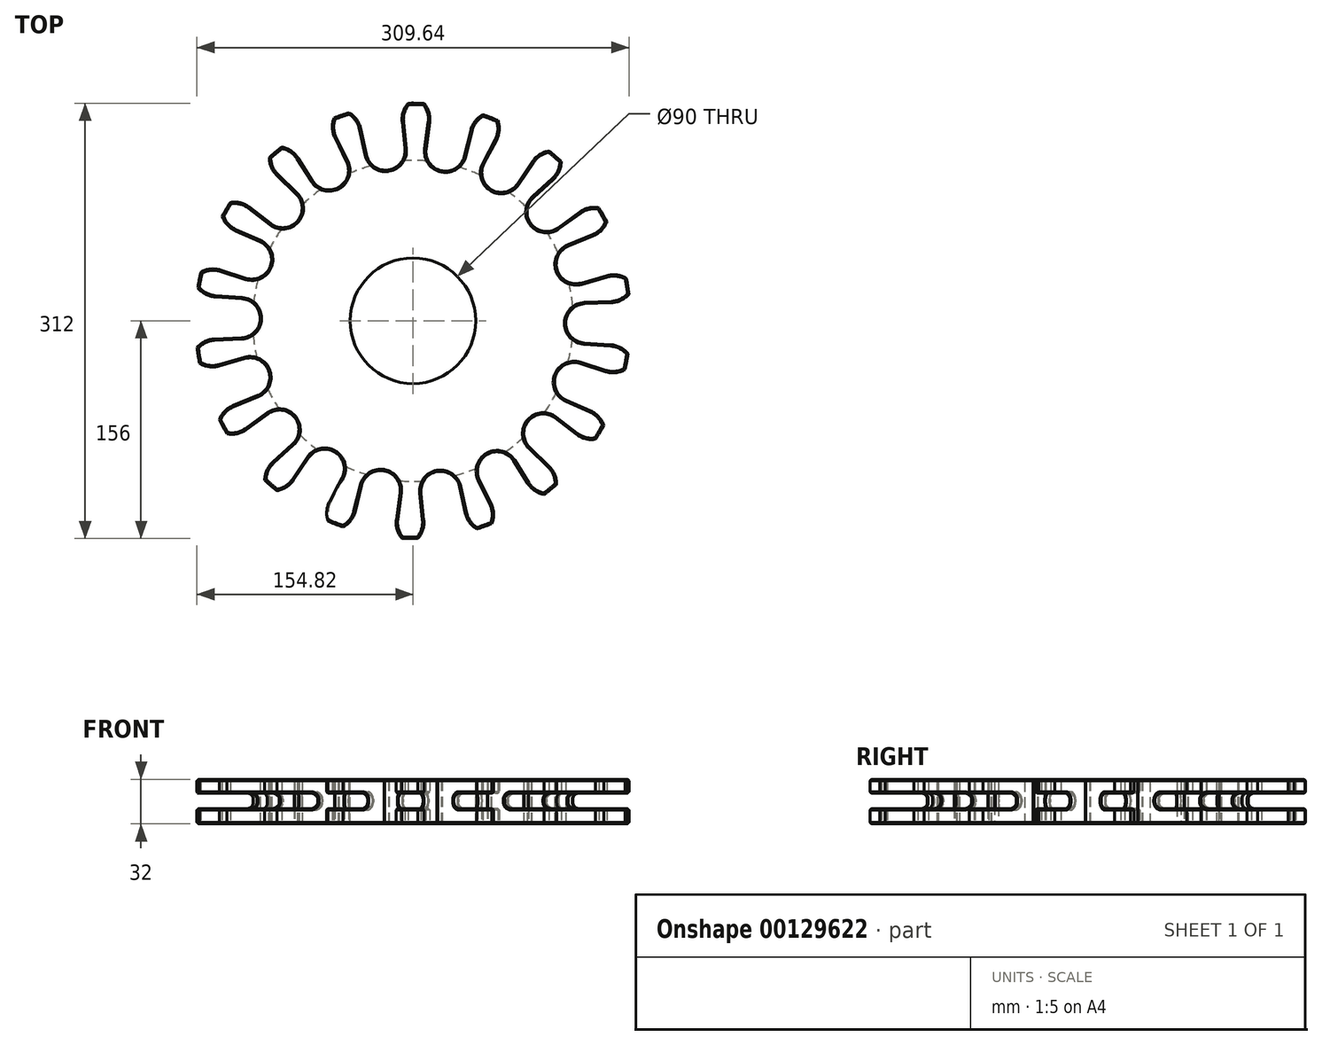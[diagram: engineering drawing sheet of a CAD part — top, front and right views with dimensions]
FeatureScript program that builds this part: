
annotation { "Feature Type Name" : "Feature", "Feature Type Description" : "" }
export const myFeature = defineFeature(function(context is Context, id is Id, definition is map)
    precondition{}
    {
        {
            var Q0;
            Q0=qCreatedBy(makeId("Top.planeOp"),FACE);
            var sketch = newSketch(context, id + "F0", { "sketchPlane" : qUnion([Q0])});
            skCircle(sketch, "E0", {"center": v(0, 0) * mm, "radius": 158.3 * mm, "construction": true});
            skArc(sketch, "E1", {"start": v(-102.28, 39.14) * mm, "mid": v(-102.55, 49.4) * mm, "end": v(-109.74, 56.72) * mm});
            skLineSegment(sketch, "E2", {"start": v(-109.74, 56.72) * mm, "end": v(-127.33, 64.55) * mm});
            skArc(sketch, "E3", {"start": v(-127.33, 64.55) * mm, "mid": v(-133.16, 68.77) * mm, "end": v(-136.8, 74.97) * mm});
            skArc(sketch, "E4", {"start": v(-136.8, 74.97) * mm, "mid": v(-133.95, 79.96) * mm, "end": v(-130.91, 84.84) * mm});
            skArc(sketch, "E5", {"start": v(-130.91, 84.84) * mm, "mid": v(-123.72, 84.58) * mm, "end": v(-117.25, 81.44) * mm});
            skLineSegment(sketch, "E6", {"start": v(-117.25, 81.44) * mm, "end": v(-102, 69.68) * mm});
            skArc(sketch, "E7", {"start": v(-102, 69.68) * mm, "mid": v(-92.15, 66.82) * mm, "end": v(-83, 71.46) * mm});
            skLineSegment(sketch, "E8", {"start": v(-83, 71.46) * mm, "end": v(-82.72, 71.76) * mm});
            skArc(sketch, "E9", {"start": v(-82.72, 71.76) * mm, "mid": v(-79.47, 81.5) * mm, "end": v(-83.72, 90.83) * mm});
            skLineSegment(sketch, "E10", {"start": v(-83.72, 90.83) * mm, "end": v(-97.57, 104.2) * mm});
            skArc(sketch, "E11", {"start": v(-97.57, 104.2) * mm, "mid": v(-101.6, 110.16) * mm, "end": v(-102.91, 117.24) * mm});
            skArc(sketch, "E12", {"start": v(-102.91, 117.24) * mm, "mid": v(-98.52, 120.95) * mm, "end": v(-94, 124.5) * mm});
            skArc(sketch, "E13", {"start": v(-94, 124.5) * mm, "mid": v(-87.33, 121.8) * mm, "end": v(-82.32, 116.63) * mm});
            skLineSegment(sketch, "E14", {"start": v(-82.32, 116.63) * mm, "end": v(-72.02, 100.36) * mm});
            skArc(sketch, "E15", {"start": v(-72.02, 100.36) * mm, "mid": v(-63.74, 94.31) * mm, "end": v(-53.55, 95.53) * mm});
            skLineSegment(sketch, "E16", {"start": v(-53.55, 95.53) * mm, "end": v(-53.2, 95.73) * mm});
            skArc(sketch, "E17", {"start": v(-53.2, 95.73) * mm, "mid": v(-46.8, 103.76) * mm, "end": v(-47.6, 113.99) * mm});
            skLineSegment(sketch, "E18", {"start": v(-47.6, 113.99) * mm, "end": v(-56.04, 131.3) * mm});
            skArc(sketch, "E19", {"start": v(-56.04, 131.3) * mm, "mid": v(-57.8, 138.27) * mm, "end": v(-56.6, 145.37) * mm});
            skArc(sketch, "E20", {"start": v(-56.6, 145.37) * mm, "mid": v(-51.21, 147.35) * mm, "end": v(-45.75, 149.14) * mm});
            skArc(sketch, "E21", {"start": v(-45.75, 149.14) * mm, "mid": v(-40.41, 144.32) * mm, "end": v(-37.46, 137.75) * mm});
            skLineSegment(sketch, "E22", {"start": v(-37.46, 137.75) * mm, "end": v(-33.35, 118.94) * mm});
            skArc(sketch, "E23", {"start": v(-33.35, 118.94) * mm, "mid": v(-27.64, 110.42) * mm, "end": v(-17.64, 108.08) * mm});
            skLineSegment(sketch, "E24", {"start": v(-17.64, 108.08) * mm, "end": v(-17.24, 108.15) * mm});
            skArc(sketch, "E25", {"start": v(-17.24, 108.15) * mm, "mid": v(-8.5, 113.5) * mm, "end": v(-5.75, 123.4) * mm});
            skLineSegment(sketch, "E26", {"start": v(-5.75, 123.4) * mm, "end": v(-7.76, 142.55) * mm});
            skArc(sketch, "E27", {"start": v(-7.76, 142.55) * mm, "mid": v(-7.02, 149.7) * mm, "end": v(-3.48, 155.96) * mm});
            skArc(sketch, "E28", {"start": v(-3.48, 155.96) * mm, "mid": v(2.27, 155.98) * mm, "end": v(8.02, 155.8) * mm});
            skArc(sketch, "E29", {"start": v(8.02, 155.8) * mm, "mid": v(11.38, 149.43) * mm, "end": v(11.9, 142.26) * mm});
            skLineSegment(sketch, "E30", {"start": v(11.9, 142.26) * mm, "end": v(9.34, 123.18) * mm});
            skArc(sketch, "E31", {"start": v(9.34, 123.18) * mm, "mid": v(11.8, 113.21) * mm, "end": v(20.39, 107.6) * mm});
            skLineSegment(sketch, "E32", {"start": v(20.39, 107.6) * mm, "end": v(20.79, 107.52) * mm});
            skArc(sketch, "E33", {"start": v(20.79, 107.52) * mm, "mid": v(30.84, 109.57) * mm, "end": v(36.8, 117.92) * mm});
            skLineSegment(sketch, "E34", {"start": v(36.8, 117.92) * mm, "end": v(41.46, 136.6) * mm});
            skArc(sketch, "E35", {"start": v(41.46, 136.6) * mm, "mid": v(44.6, 143.08) * mm, "end": v(50.07, 147.74) * mm});
            skArc(sketch, "E36", {"start": v(50.07, 147.74) * mm, "mid": v(55.49, 145.8) * mm, "end": v(60.82, 143.65) * mm});
            skArc(sketch, "E37", {"start": v(60.82, 143.65) * mm, "mid": v(61.8, 136.53) * mm, "end": v(59.85, 129.6) * mm});
            skLineSegment(sketch, "E38", {"start": v(59.85, 129.6) * mm, "end": v(50.9, 112.55) * mm});
            skArc(sketch, "E39", {"start": v(50.9, 112.55) * mm, "mid": v(49.8, 102.35) * mm, "end": v(55.96, 94.14) * mm});
            skLineSegment(sketch, "E40", {"start": v(55.96, 94.14) * mm, "end": v(56.3, 93.93) * mm});
            skArc(sketch, "E41", {"start": v(56.3, 93.93) * mm, "mid": v(66.46, 92.41) * mm, "end": v(74.91, 98.22) * mm});
            skLineSegment(sketch, "E42", {"start": v(74.91, 98.22) * mm, "end": v(85.68, 114.18) * mm});
            skArc(sketch, "E43", {"start": v(85.68, 114.18) * mm, "mid": v(90.85, 119.2) * mm, "end": v(97.59, 121.7) * mm});
            skArc(sketch, "E44", {"start": v(97.59, 121.7) * mm, "mid": v(102, 118.03) * mm, "end": v(106.29, 114.19) * mm});
            skArc(sketch, "E45", {"start": v(106.29, 114.19) * mm, "mid": v(104.77, 107.16) * mm, "end": v(100.56, 101.32) * mm});
            skLineSegment(sketch, "E46", {"start": v(100.56, 101.32) * mm, "end": v(86.33, 88.35) * mm});
            skArc(sketch, "E47", {"start": v(86.33, 88.35) * mm, "mid": v(81.8, 79.14) * mm, "end": v(84.78, 69.32) * mm});
            skLineSegment(sketch, "E48", {"start": v(84.78, 69.32) * mm, "end": v(85.04, 69) * mm});
            skArc(sketch, "E49", {"start": v(85.04, 69) * mm, "mid": v(94.06, 64.1) * mm, "end": v(104, 66.68) * mm});
            skLineSegment(sketch, "E50", {"start": v(104, 66.68) * mm, "end": v(119.57, 78) * mm});
            skArc(sketch, "E51", {"start": v(119.57, 78) * mm, "mid": v(126.13, 80.93) * mm, "end": v(133.33, 81) * mm});
            skArc(sketch, "E52", {"start": v(133.33, 81) * mm, "mid": v(136.22, 76.02) * mm, "end": v(138.93, 70.95) * mm});
            skArc(sketch, "E53", {"start": v(138.93, 70.95) * mm, "mid": v(135.1, 64.86) * mm, "end": v(129.15, 60.82) * mm});
            skLineSegment(sketch, "E54", {"start": v(129.15, 60.82) * mm, "end": v(111.35, 53.5) * mm});
            skArc(sketch, "E55", {"start": v(111.35, 53.5) * mm, "mid": v(103.94, 46.4) * mm, "end": v(103.38, 36.15) * mm});
            skLineSegment(sketch, "E56", {"start": v(103.38, 36.15) * mm, "end": v(103.51, 35.76) * mm});
            skArc(sketch, "E57", {"start": v(103.51, 35.76) * mm, "mid": v(110.31, 28.07) * mm, "end": v(120.52, 27.09) * mm});
            skLineSegment(sketch, "E58", {"start": v(120.52, 27.09) * mm, "end": v(139.03, 32.4) * mm});
            skArc(sketch, "E59", {"start": v(139.03, 32.4) * mm, "mid": v(146.2, 32.91) * mm, "end": v(152.99, 30.5) * mm});
            skArc(sketch, "E60", {"start": v(152.99, 30.5) * mm, "mid": v(154, 24.85) * mm, "end": v(154.82, 19.15) * mm});
            skArc(sketch, "E61", {"start": v(154.82, 19.15) * mm, "mid": v(149.14, 14.74) * mm, "end": v(142.17, 12.98) * mm});
            skLineSegment(sketch, "E62", {"start": v(142.17, 12.98) * mm, "end": v(122.93, 12.19) * mm});
            skArc(sketch, "E63", {"start": v(122.93, 12.19) * mm, "mid": v(113.54, 8.04) * mm, "end": v(109.5, -1.4) * mm});
            skLineSegment(sketch, "E64", {"start": v(109.5, -1.4) * mm, "end": v(109.5, -1.8) * mm});
            skArc(sketch, "E65", {"start": v(109.5, -1.8) * mm, "mid": v(113.26, -11.35) * mm, "end": v(122.52, -15.77) * mm});
            skLineSegment(sketch, "E66", {"start": v(122.52, -15.77) * mm, "end": v(141.73, -17.11) * mm});
            skArc(sketch, "E67", {"start": v(141.73, -17.11) * mm, "mid": v(148.65, -19.08) * mm, "end": v(154.2, -23.66) * mm});
            skArc(sketch, "E68", {"start": v(154.2, -23.66) * mm, "mid": v(153.22, -29.33) * mm, "end": v(152.03, -34.95) * mm});
            skArc(sketch, "E69", {"start": v(152.03, -34.95) * mm, "mid": v(145.19, -37.16) * mm, "end": v(138.03, -36.43) * mm});
            skLineSegment(sketch, "E70", {"start": v(138.03, -36.43) * mm, "end": v(119.68, -30.6) * mm});
            skArc(sketch, "E71", {"start": v(119.68, -30.6) * mm, "mid": v(109.45, -31.28) * mm, "end": v(102.43, -38.76) * mm});
            skLineSegment(sketch, "E72", {"start": v(102.43, -38.76) * mm, "end": v(102.28, -39.14) * mm});
            skArc(sketch, "E73", {"start": v(102.28, -39.14) * mm, "mid": v(102.55, -49.4) * mm, "end": v(109.74, -56.72) * mm});
            skLineSegment(sketch, "E74", {"start": v(109.74, -56.72) * mm, "end": v(127.33, -64.55) * mm});
            skArc(sketch, "E75", {"start": v(127.33, -64.55) * mm, "mid": v(133.16, -68.77) * mm, "end": v(136.8, -74.97) * mm});
            skArc(sketch, "E76", {"start": v(136.8, -74.97) * mm, "mid": v(133.95, -79.96) * mm, "end": v(130.91, -84.84) * mm});
            skArc(sketch, "E77", {"start": v(130.91, -84.84) * mm, "mid": v(123.72, -84.58) * mm, "end": v(117.25, -81.44) * mm});
            skLineSegment(sketch, "E78", {"start": v(117.25, -81.44) * mm, "end": v(102, -69.68) * mm});
            skArc(sketch, "E79", {"start": v(102, -69.68) * mm, "mid": v(92.15, -66.82) * mm, "end": v(83, -71.46) * mm});
            skLineSegment(sketch, "E80", {"start": v(83, -71.46) * mm, "end": v(82.72, -71.76) * mm});
            skArc(sketch, "E81", {"start": v(82.72, -71.76) * mm, "mid": v(79.47, -81.5) * mm, "end": v(83.72, -90.83) * mm});
            skLineSegment(sketch, "E82", {"start": v(83.72, -90.83) * mm, "end": v(97.57, -104.2) * mm});
            skArc(sketch, "E83", {"start": v(97.57, -104.2) * mm, "mid": v(101.6, -110.16) * mm, "end": v(102.91, -117.24) * mm});
            skArc(sketch, "E84", {"start": v(102.91, -117.24) * mm, "mid": v(98.52, -120.95) * mm, "end": v(94, -124.5) * mm});
            skArc(sketch, "E85", {"start": v(94, -124.5) * mm, "mid": v(87.33, -121.8) * mm, "end": v(82.32, -116.63) * mm});
            skLineSegment(sketch, "E86", {"start": v(82.32, -116.63) * mm, "end": v(72.02, -100.36) * mm});
            skArc(sketch, "E87", {"start": v(72.02, -100.36) * mm, "mid": v(63.74, -94.31) * mm, "end": v(53.55, -95.53) * mm});
            skLineSegment(sketch, "E88", {"start": v(53.55, -95.53) * mm, "end": v(53.2, -95.73) * mm});
            skArc(sketch, "E89", {"start": v(53.2, -95.73) * mm, "mid": v(46.8, -103.76) * mm, "end": v(47.6, -113.99) * mm});
            skLineSegment(sketch, "E90", {"start": v(47.6, -113.99) * mm, "end": v(56.04, -131.3) * mm});
            skArc(sketch, "E91", {"start": v(56.04, -131.3) * mm, "mid": v(57.8, -138.27) * mm, "end": v(56.6, -145.37) * mm});
            skArc(sketch, "E92", {"start": v(56.6, -145.37) * mm, "mid": v(51.21, -147.35) * mm, "end": v(45.75, -149.14) * mm});
            skArc(sketch, "E93", {"start": v(45.75, -149.14) * mm, "mid": v(40.41, -144.32) * mm, "end": v(37.46, -137.75) * mm});
            skLineSegment(sketch, "E94", {"start": v(37.46, -137.75) * mm, "end": v(33.35, -118.94) * mm});
            skArc(sketch, "E95", {"start": v(33.35, -118.94) * mm, "mid": v(27.64, -110.42) * mm, "end": v(17.64, -108.08) * mm});
            skLineSegment(sketch, "E96", {"start": v(17.64, -108.08) * mm, "end": v(17.24, -108.15) * mm});
            skArc(sketch, "E97", {"start": v(17.24, -108.15) * mm, "mid": v(8.5, -113.5) * mm, "end": v(5.75, -123.4) * mm});
            skLineSegment(sketch, "E98", {"start": v(5.75, -123.4) * mm, "end": v(7.76, -142.55) * mm});
            skArc(sketch, "E99", {"start": v(7.76, -142.55) * mm, "mid": v(7.02, -149.7) * mm, "end": v(3.48, -155.96) * mm});
            skArc(sketch, "E100", {"start": v(3.48, -155.96) * mm, "mid": v(-2.27, -155.98) * mm, "end": v(-8.02, -155.8) * mm});
            skArc(sketch, "E101", {"start": v(-8.02, -155.8) * mm, "mid": v(-11.38, -149.43) * mm, "end": v(-11.9, -142.26) * mm});
            skLineSegment(sketch, "E102", {"start": v(-11.9, -142.26) * mm, "end": v(-9.34, -123.18) * mm});
            skArc(sketch, "E103", {"start": v(-9.34, -123.18) * mm, "mid": v(-11.8, -113.21) * mm, "end": v(-20.39, -107.6) * mm});
            skLineSegment(sketch, "E104", {"start": v(-20.39, -107.6) * mm, "end": v(-20.79, -107.52) * mm});
            skArc(sketch, "E105", {"start": v(-20.79, -107.52) * mm, "mid": v(-30.84, -109.57) * mm, "end": v(-36.8, -117.92) * mm});
            skLineSegment(sketch, "E106", {"start": v(-36.8, -117.92) * mm, "end": v(-41.46, -136.6) * mm});
            skArc(sketch, "E107", {"start": v(-41.46, -136.6) * mm, "mid": v(-44.6, -143.08) * mm, "end": v(-50.07, -147.74) * mm});
            skArc(sketch, "E108", {"start": v(-50.07, -147.74) * mm, "mid": v(-55.49, -145.8) * mm, "end": v(-60.82, -143.65) * mm});
            skArc(sketch, "E109", {"start": v(-60.82, -143.65) * mm, "mid": v(-61.8, -136.53) * mm, "end": v(-59.85, -129.6) * mm});
            skLineSegment(sketch, "E110", {"start": v(-59.85, -129.6) * mm, "end": v(-50.9, -112.55) * mm});
            skArc(sketch, "E111", {"start": v(-50.9, -112.55) * mm, "mid": v(-49.8, -102.35) * mm, "end": v(-55.96, -94.14) * mm});
            skLineSegment(sketch, "E112", {"start": v(-55.96, -94.14) * mm, "end": v(-56.3, -93.93) * mm});
            skArc(sketch, "E113", {"start": v(-56.3, -93.93) * mm, "mid": v(-66.46, -92.41) * mm, "end": v(-74.91, -98.22) * mm});
            skLineSegment(sketch, "E114", {"start": v(-74.91, -98.22) * mm, "end": v(-85.68, -114.18) * mm});
            skArc(sketch, "E115", {"start": v(-85.68, -114.18) * mm, "mid": v(-90.85, -119.2) * mm, "end": v(-97.59, -121.7) * mm});
            skArc(sketch, "E116", {"start": v(-97.59, -121.7) * mm, "mid": v(-102, -118.03) * mm, "end": v(-106.29, -114.19) * mm});
            skArc(sketch, "E117", {"start": v(-106.29, -114.19) * mm, "mid": v(-104.77, -107.16) * mm, "end": v(-100.56, -101.32) * mm});
            skLineSegment(sketch, "E118", {"start": v(-100.56, -101.32) * mm, "end": v(-86.33, -88.35) * mm});
            skArc(sketch, "E119", {"start": v(-86.33, -88.35) * mm, "mid": v(-81.8, -79.14) * mm, "end": v(-84.78, -69.32) * mm});
            skLineSegment(sketch, "E120", {"start": v(-84.78, -69.32) * mm, "end": v(-85.04, -69) * mm});
            skArc(sketch, "E121", {"start": v(-85.04, -69) * mm, "mid": v(-94.06, -64.1) * mm, "end": v(-104, -66.68) * mm});
            skLineSegment(sketch, "E122", {"start": v(-104, -66.68) * mm, "end": v(-119.57, -78) * mm});
            skArc(sketch, "E123", {"start": v(-119.57, -78) * mm, "mid": v(-126.13, -80.93) * mm, "end": v(-133.33, -81) * mm});
            skArc(sketch, "E124", {"start": v(-133.33, -81) * mm, "mid": v(-136.22, -76.02) * mm, "end": v(-138.93, -70.95) * mm});
            skArc(sketch, "E125", {"start": v(-138.93, -70.95) * mm, "mid": v(-135.1, -64.86) * mm, "end": v(-129.15, -60.82) * mm});
            skLineSegment(sketch, "E126", {"start": v(-129.15, -60.82) * mm, "end": v(-111.35, -53.5) * mm});
            skArc(sketch, "E127", {"start": v(-111.35, -53.5) * mm, "mid": v(-103.94, -46.4) * mm, "end": v(-103.38, -36.15) * mm});
            skLineSegment(sketch, "E128", {"start": v(-103.38, -36.15) * mm, "end": v(-103.51, -35.76) * mm});
            skArc(sketch, "E129", {"start": v(-103.51, -35.76) * mm, "mid": v(-110.31, -28.07) * mm, "end": v(-120.52, -27.09) * mm});
            skLineSegment(sketch, "E130", {"start": v(-120.52, -27.09) * mm, "end": v(-139.03, -32.4) * mm});
            skArc(sketch, "E131", {"start": v(-139.03, -32.4) * mm, "mid": v(-146.2, -32.91) * mm, "end": v(-152.99, -30.5) * mm});
            skArc(sketch, "E132", {"start": v(-152.99, -30.5) * mm, "mid": v(-154, -24.85) * mm, "end": v(-154.82, -19.15) * mm});
            skArc(sketch, "E133", {"start": v(-154.82, -19.15) * mm, "mid": v(-149.14, -14.74) * mm, "end": v(-142.17, -12.98) * mm});
            skLineSegment(sketch, "E134", {"start": v(-142.17, -12.98) * mm, "end": v(-122.93, -12.19) * mm});
            skArc(sketch, "E135", {"start": v(-122.93, -12.19) * mm, "mid": v(-113.54, -8.04) * mm, "end": v(-109.5, 1.4) * mm});
            skLineSegment(sketch, "E136", {"start": v(-109.5, 1.4) * mm, "end": v(-109.5, 1.8) * mm});
            skArc(sketch, "E137", {"start": v(-109.5, 1.8) * mm, "mid": v(-113.26, 11.35) * mm, "end": v(-122.52, 15.77) * mm});
            skLineSegment(sketch, "E138", {"start": v(-122.52, 15.77) * mm, "end": v(-141.73, 17.11) * mm});
            skArc(sketch, "E139", {"start": v(-141.73, 17.11) * mm, "mid": v(-148.65, 19.08) * mm, "end": v(-154.2, 23.66) * mm});
            skArc(sketch, "E140", {"start": v(-154.2, 23.66) * mm, "mid": v(-153.22, 29.33) * mm, "end": v(-152.03, 34.95) * mm});
            skArc(sketch, "E141", {"start": v(-152.03, 34.95) * mm, "mid": v(-145.19, 37.16) * mm, "end": v(-138.03, 36.43) * mm});
            skLineSegment(sketch, "E142", {"start": v(-138.03, 36.43) * mm, "end": v(-119.68, 30.6) * mm});
            skArc(sketch, "E143", {"start": v(-119.68, 30.6) * mm, "mid": v(-109.45, 31.28) * mm, "end": v(-102.43, 38.76) * mm});
            skLineSegment(sketch, "E144", {"start": v(-102.43, 38.76) * mm, "end": v(-102.28, 39.14) * mm});
            skCircle(sketch, "E145", {"center": v(0, 0) * mm, "radius": 74.9 * mm, "construction": true});
            skSolve(sketch);
        }
        {
            var Q0;
            Q0 = qSketchRegion(id + "F0", true);
            extrude(context, id + "F1", {"entities" : qUnion([Q0]), "endBound" : BoundingType.SYMMETRIC, "depth" : 32 * mm});
        }
        {
            var Q0;
            Q0=qCreatedBy(makeId("Top.planeOp"),FACE);
            var sketch = newSketch(context, id + "F2", { "sketchPlane" : qUnion([Q0])});
            skCircle(sketch, "E146", {"center": v(0, 0) * mm, "radius": 45 * mm});
            skSolve(sketch);
        }
        {
            var Q0;
            Q0 = qSketchRegion(id + "F2", true);
            extrude(context, id + "F3", {"entities" : qUnion([Q0]), "operationType" : NewBodyOperationType.REMOVE, "endBound" : BoundingType.SYMMETRIC, "oppositeDirection" : true, "depth" : 91.5 * mm});
        }
        {
            var Q0;
            Q0=qCreatedBy(makeId("Right.planeOp"),FACE);
            var sketch = newSketch(context, id + "F4", { "sketchPlane" : qUnion([Q0])});
            skLineSegment(sketch, "E147.bottom", {"start": v(-163.5, 6) * mm, "end": v(-119.5, 6) * mm});
            skLineSegment(sketch, "E147.top", {"start": v(-163.5, -5) * mm, "end": v(-119.5, -5) * mm});
            skLineSegment(sketch, "E147.left", {"start": v(-163.5, 6) * mm, "end": v(-163.5, -5) * mm});
            skLineSegment(sketch, "E147.right", {"start": v(-115, 1.5) * mm, "end": v(-115, -0.5) * mm});
            skPoint(sketch, "E148.visualSharp", {"position": v(-115, 6) * mm});
            skArc(sketch, "E148.filletArc", {"start": v(-115, 1.5) * mm, "mid": v(-116.32, 4.68) * mm, "end": v(-119.5, 6) * mm});
            skPoint(sketch, "E149.visualSharp", {"position": v(-115, -5) * mm});
            skArc(sketch, "E149.filletArc", {"start": v(-119.5, -5) * mm, "mid": v(-116.32, -3.68) * mm, "end": v(-115, -0.5) * mm});
            skSolve(sketch);
        }
        {
            var Q0;
            Q0 = qSketchRegion(id + "F4", true);
            var Q1;
            Q1=makeQuery(id+"F3.boolean.opBoolean","COPY",FACE,{"derivedFrom":makeQuery(id+"F3.opExtrude","SWEPT_FACE",FACE,{"disambiguationData":[OSD([sQuery(id+"F2.wireOp",EDGE,"E146")])]})});
            revolve(context, id + "F5", {"operationType" : NewBodyOperationType.REMOVE, "entities" : qUnion([Q0]), "axis" : qUnion([Q1]), "revolveType" : RevolveType.FULL, "oppositeDirection" : true});
        }
        {
            var Q0;
            Q0=makeQuery(id+"F1.opExtrude","CAP_EDGE",EDGE,{"disambiguationData":[OSD([sQuery(id+"F0.wireOp",EDGE,"E113")])],"isStart":false});
            var Q1;
            Q1=makeQuery(id+"F1.opExtrude","CAP_EDGE",EDGE,{"disambiguationData":[OSD([sQuery(id+"F0.wireOp",EDGE,"E121")])],"isStart":false});
            var Q2;
            Q2=makeQuery(id+"F1.opExtrude","CAP_EDGE",EDGE,{"disambiguationData":[OSD([sQuery(id+"F0.wireOp",EDGE,"E129")])],"isStart":false});
            var Q3;
            Q3=makeQuery(id+"F1.opExtrude","CAP_EDGE",EDGE,{"disambiguationData":[OSD([sQuery(id+"F0.wireOp",EDGE,"E137")])],"isStart":false});
            var Q4;
            Q4=makeQuery(id+"F1.opExtrude","CAP_EDGE",EDGE,{"disambiguationData":[OSD([sQuery(id+"F0.wireOp",EDGE,"E1")])],"isStart":false});
            var Q5;
            Q5=makeQuery(id+"F1.opExtrude","CAP_EDGE",EDGE,{"disambiguationData":[OSD([sQuery(id+"F0.wireOp",EDGE,"E9")])],"isStart":false});
            var Q6;
            Q6=makeQuery(id+"F1.opExtrude","CAP_EDGE",EDGE,{"disambiguationData":[OSD([sQuery(id+"F0.wireOp",EDGE,"E17")])],"isStart":false});
            var Q7;
            Q7=makeQuery(id+"F1.opExtrude","CAP_EDGE",EDGE,{"disambiguationData":[OSD([sQuery(id+"F0.wireOp",EDGE,"E25")])],"isStart":false});
            var Q8;
            Q8=makeQuery(id+"F1.opExtrude","CAP_EDGE",EDGE,{"disambiguationData":[OSD([sQuery(id+"F0.wireOp",EDGE,"E33")])],"isStart":false});
            var Q9;
            Q9=makeQuery(id+"F1.opExtrude","CAP_EDGE",EDGE,{"disambiguationData":[OSD([sQuery(id+"F0.wireOp",EDGE,"E41")])],"isStart":false});
            var Q10;
            Q10=makeQuery(id+"F1.opExtrude","CAP_EDGE",EDGE,{"disambiguationData":[OSD([sQuery(id+"F0.wireOp",EDGE,"E50")])],"isStart":false});
            var Q11;
            Q11=makeQuery(id+"F1.opExtrude","CAP_EDGE",EDGE,{"disambiguationData":[OSD([sQuery(id+"F0.wireOp",EDGE,"E58")])],"isStart":false});
            var Q12;
            Q12=makeQuery(id+"F1.opExtrude","CAP_EDGE",EDGE,{"disambiguationData":[OSD([sQuery(id+"F0.wireOp",EDGE,"E65")])],"isStart":false});
            var Q13;
            Q13=makeQuery(id+"F1.opExtrude","CAP_EDGE",EDGE,{"disambiguationData":[OSD([sQuery(id+"F0.wireOp",EDGE,"E73")])],"isStart":false});
            var Q14;
            Q14=makeQuery(id+"F1.opExtrude","CAP_EDGE",EDGE,{"disambiguationData":[OSD([sQuery(id+"F0.wireOp",EDGE,"E81")])],"isStart":false});
            var Q15;
            Q15=makeQuery(id+"F1.opExtrude","CAP_EDGE",EDGE,{"disambiguationData":[OSD([sQuery(id+"F0.wireOp",EDGE,"E89")])],"isStart":false});
            var Q16;
            Q16=makeQuery(id+"F1.opExtrude","CAP_EDGE",EDGE,{"disambiguationData":[OSD([sQuery(id+"F0.wireOp",EDGE,"E97")])],"isStart":false});
            var Q17;
            Q17=makeQuery(id+"F1.opExtrude","CAP_EDGE",EDGE,{"disambiguationData":[OSD([sQuery(id+"F0.wireOp",EDGE,"E105")])],"isStart":false});
            var Q18;
            Q18=makeQuery(id+"F1.opExtrude","CAP_EDGE",EDGE,{"disambiguationData":[OSD([sQuery(id+"F0.wireOp",EDGE,"E103")])],"isStart":false});
            var Q19;
            Q19=makeQuery(id+"F1.opExtrude","CAP_EDGE",EDGE,{"disambiguationData":[OSD([sQuery(id+"F0.wireOp",EDGE,"E95")])],"isStart":false});
            var Q20;
            Q20=makeQuery(id+"F1.opExtrude","CAP_EDGE",EDGE,{"disambiguationData":[OSD([sQuery(id+"F0.wireOp",EDGE,"E87")])],"isStart":false});
            var Q21;
            Q21=makeQuery(id+"F1.opExtrude","CAP_EDGE",EDGE,{"disambiguationData":[OSD([sQuery(id+"F0.wireOp",EDGE,"E79")])],"isStart":false});
            var Q22;
            Q22=makeQuery(id+"F1.opExtrude","CAP_EDGE",EDGE,{"disambiguationData":[OSD([sQuery(id+"F0.wireOp",EDGE,"E71")])],"isStart":false});
            var Q23;
            Q23=makeQuery(id+"F1.opExtrude","CAP_EDGE",EDGE,{"disambiguationData":[OSD([sQuery(id+"F0.wireOp",EDGE,"E63")])],"isStart":false});
            var Q24;
            Q24=makeQuery(id+"F1.opExtrude","CAP_EDGE",EDGE,{"disambiguationData":[OSD([sQuery(id+"F0.wireOp",EDGE,"E55")])],"isStart":false});
            var Q25;
            Q25=makeQuery(id+"F1.opExtrude","CAP_EDGE",EDGE,{"disambiguationData":[OSD([sQuery(id+"F0.wireOp",EDGE,"E47")])],"isStart":false});
            var Q26;
            Q26=makeQuery(id+"F1.opExtrude","CAP_EDGE",EDGE,{"disambiguationData":[OSD([sQuery(id+"F0.wireOp",EDGE,"E119")])],"isStart":false});
            var Q27;
            Q27=makeQuery(id+"F1.opExtrude","CAP_EDGE",EDGE,{"disambiguationData":[OSD([sQuery(id+"F0.wireOp",EDGE,"E127")])],"isStart":false});
            var Q28;
            Q28=makeQuery(id+"F1.opExtrude","CAP_EDGE",EDGE,{"disambiguationData":[OSD([sQuery(id+"F0.wireOp",EDGE,"E135")])],"isStart":false});
            var Q29;
            Q29=makeQuery(id+"F1.opExtrude","CAP_EDGE",EDGE,{"disambiguationData":[OSD([sQuery(id+"F0.wireOp",EDGE,"E143")])],"isStart":false});
            var Q30;
            Q30=makeQuery(id+"F1.opExtrude","CAP_EDGE",EDGE,{"disambiguationData":[OSD([sQuery(id+"F0.wireOp",EDGE,"E7")])],"isStart":false});
            var Q31;
            Q31=makeQuery(id+"F1.opExtrude","CAP_EDGE",EDGE,{"disambiguationData":[OSD([sQuery(id+"F0.wireOp",EDGE,"E15")])],"isStart":false});
            var Q32;
            Q32=makeQuery(id+"F1.opExtrude","CAP_EDGE",EDGE,{"disambiguationData":[OSD([sQuery(id+"F0.wireOp",EDGE,"E23")])],"isStart":false});
            var Q33;
            Q33=makeQuery(id+"F1.opExtrude","CAP_EDGE",EDGE,{"disambiguationData":[OSD([sQuery(id+"F0.wireOp",EDGE,"E31")])],"isStart":false});
            var Q34;
            Q34=makeQuery(id+"F1.opExtrude","CAP_EDGE",EDGE,{"disambiguationData":[OSD([sQuery(id+"F0.wireOp",EDGE,"E39")])],"isStart":false});
            var Q35;
            Q35=makeQuery(id+"F1.opExtrude","CAP_EDGE",EDGE,{"disambiguationData":[OSD([sQuery(id+"F0.wireOp",EDGE,"E100")])],"isStart":false});
            var Q36;
            Q36=makeQuery(id+"F1.opExtrude","CAP_EDGE",EDGE,{"disambiguationData":[OSD([sQuery(id+"F0.wireOp",EDGE,"E108")])],"isStart":false});
            var Q37;
            Q37=makeQuery(id+"F1.opExtrude","CAP_EDGE",EDGE,{"disambiguationData":[OSD([sQuery(id+"F0.wireOp",EDGE,"E116")])],"isStart":false});
            var Q38;
            Q38=makeQuery(id+"F1.opExtrude","CAP_EDGE",EDGE,{"disambiguationData":[OSD([sQuery(id+"F0.wireOp",EDGE,"E124")])],"isStart":false});
            var Q39;
            Q39=makeQuery(id+"F1.opExtrude","CAP_EDGE",EDGE,{"disambiguationData":[OSD([sQuery(id+"F0.wireOp",EDGE,"E132")])],"isStart":false});
            var Q40;
            Q40=makeQuery(id+"F1.opExtrude","CAP_EDGE",EDGE,{"disambiguationData":[OSD([sQuery(id+"F0.wireOp",EDGE,"E140")])],"isStart":false});
            var Q41;
            Q41=makeQuery(id+"F1.opExtrude","CAP_EDGE",EDGE,{"disambiguationData":[OSD([sQuery(id+"F0.wireOp",EDGE,"E4")])],"isStart":false});
            var Q42;
            Q42=makeQuery(id+"F1.opExtrude","CAP_EDGE",EDGE,{"disambiguationData":[OSD([sQuery(id+"F0.wireOp",EDGE,"E12")])],"isStart":false});
            var Q43;
            Q43=makeQuery(id+"F1.opExtrude","CAP_EDGE",EDGE,{"disambiguationData":[OSD([sQuery(id+"F0.wireOp",EDGE,"E20")])],"isStart":false});
            var Q44;
            Q44=makeQuery(id+"F1.opExtrude","CAP_EDGE",EDGE,{"disambiguationData":[OSD([sQuery(id+"F0.wireOp",EDGE,"E28")])],"isStart":false});
            var Q45;
            Q45=makeQuery(id+"F1.opExtrude","CAP_EDGE",EDGE,{"disambiguationData":[OSD([sQuery(id+"F0.wireOp",EDGE,"E36")])],"isStart":false});
            var Q46;
            Q46=makeQuery(id+"F1.opExtrude","CAP_EDGE",EDGE,{"disambiguationData":[OSD([sQuery(id+"F0.wireOp",EDGE,"E44")])],"isStart":false});
            var Q47;
            Q47=makeQuery(id+"F1.opExtrude","CAP_EDGE",EDGE,{"disambiguationData":[OSD([sQuery(id+"F0.wireOp",EDGE,"E52")])],"isStart":false});
            var Q48;
            Q48=makeQuery(id+"F1.opExtrude","CAP_EDGE",EDGE,{"disambiguationData":[OSD([sQuery(id+"F0.wireOp",EDGE,"E60")])],"isStart":false});
            var Q49;
            Q49=makeQuery(id+"F1.opExtrude","CAP_EDGE",EDGE,{"disambiguationData":[OSD([sQuery(id+"F0.wireOp",EDGE,"E68")])],"isStart":false});
            var Q50;
            Q50=makeQuery(id+"F1.opExtrude","CAP_EDGE",EDGE,{"disambiguationData":[OSD([sQuery(id+"F0.wireOp",EDGE,"E76")])],"isStart":false});
            var Q51;
            Q51=makeQuery(id+"F1.opExtrude","CAP_EDGE",EDGE,{"disambiguationData":[OSD([sQuery(id+"F0.wireOp",EDGE,"E84")])],"isStart":false});
            var Q52;
            Q52=makeQuery(id+"F1.opExtrude","CAP_EDGE",EDGE,{"disambiguationData":[OSD([sQuery(id+"F0.wireOp",EDGE,"E92")])],"isStart":false});
            var Q53;
            Q53=makeQuery(id+"F5.boolean.opBoolean","INTERSECT",EDGE,{"derivedFrom":[makeQuery(id+"F1.opExtrude","SWEPT_FACE",FACE,{"disambiguationData":[OSD([sQuery(id+"F0.wireOp",EDGE,"E89")])]}),makeQuery(id+"F5.opRevolve","SWEPT_FACE",FACE,{"disambiguationData":[OSD([sQuery(id+"F4.wireOp",EDGE,"E149.filletArc")])]})]});
            var Q54;
            Q54=makeQuery(id+"F5.boolean.opBoolean","INTERSECT",EDGE,{"derivedFrom":[makeQuery(id+"F1.opExtrude","SWEPT_FACE",FACE,{"disambiguationData":[OSD([sQuery(id+"F0.wireOp",EDGE,"E81")])]}),makeQuery(id+"F5.opRevolve","SWEPT_FACE",FACE,{"disambiguationData":[OSD([sQuery(id+"F4.wireOp",EDGE,"E149.filletArc")])]})]});
            var Q55;
            Q55=makeQuery(id+"F5.boolean.opBoolean","INTERSECT",EDGE,{"derivedFrom":[makeQuery(id+"F1.opExtrude","SWEPT_FACE",FACE,{"disambiguationData":[OSD([sQuery(id+"F0.wireOp",EDGE,"E79")])]}),makeQuery(id+"F5.opRevolve","SWEPT_FACE",FACE,{"disambiguationData":[OSD([sQuery(id+"F4.wireOp",EDGE,"E149.filletArc")])]})]});
            var Q56;
            Q56=makeQuery(id+"F5.boolean.opBoolean","INTERSECT",EDGE,{"derivedFrom":[makeQuery(id+"F1.opExtrude","SWEPT_FACE",FACE,{"disambiguationData":[OSD([sQuery(id+"F0.wireOp",EDGE,"E87")])]}),makeQuery(id+"F5.opRevolve","SWEPT_FACE",FACE,{"disambiguationData":[OSD([sQuery(id+"F4.wireOp",EDGE,"E149.filletArc")])]})]});
            var Q57;
            Q57=makeQuery(id+"F5.boolean.opBoolean","INTERSECT",EDGE,{"derivedFrom":[makeQuery(id+"F1.opExtrude","SWEPT_FACE",FACE,{"disambiguationData":[OSD([sQuery(id+"F0.wireOp",EDGE,"E95")])]}),makeQuery(id+"F5.opRevolve","SWEPT_FACE",FACE,{"disambiguationData":[OSD([sQuery(id+"F4.wireOp",EDGE,"E149.filletArc")])]})]});
            var Q58;
            Q58=makeQuery(id+"F5.boolean.opBoolean","INTERSECT",EDGE,{"derivedFrom":[makeQuery(id+"F1.opExtrude","SWEPT_FACE",FACE,{"disambiguationData":[OSD([sQuery(id+"F0.wireOp",EDGE,"E97")])]}),makeQuery(id+"F5.opRevolve","SWEPT_FACE",FACE,{"disambiguationData":[OSD([sQuery(id+"F4.wireOp",EDGE,"E149.filletArc")])]})]});
            var Q59;
            Q59=makeQuery(id+"F5.boolean.opBoolean","INTERSECT",EDGE,{"derivedFrom":[makeQuery(id+"F1.opExtrude","SWEPT_FACE",FACE,{"disambiguationData":[OSD([sQuery(id+"F0.wireOp",EDGE,"E105")])]}),makeQuery(id+"F5.opRevolve","SWEPT_FACE",FACE,{"disambiguationData":[OSD([sQuery(id+"F4.wireOp",EDGE,"E149.filletArc")])]})]});
            var Q60;
            Q60=makeQuery(id+"F5.boolean.opBoolean","INTERSECT",EDGE,{"derivedFrom":[makeQuery(id+"F1.opExtrude","SWEPT_FACE",FACE,{"disambiguationData":[OSD([sQuery(id+"F0.wireOp",EDGE,"E103")])]}),makeQuery(id+"F5.opRevolve","SWEPT_FACE",FACE,{"disambiguationData":[OSD([sQuery(id+"F4.wireOp",EDGE,"E149.filletArc")])]})]});
            var Q61;
            Q61=makeQuery(id+"F5.boolean.opBoolean","INTERSECT",EDGE,{"derivedFrom":[makeQuery(id+"F1.opExtrude","SWEPT_FACE",FACE,{"disambiguationData":[OSD([sQuery(id+"F0.wireOp",EDGE,"E111")])]}),makeQuery(id+"F5.opRevolve","SWEPT_FACE",FACE,{"disambiguationData":[OSD([sQuery(id+"F4.wireOp",EDGE,"E149.filletArc")])]})]});
            var Q62;
            Q62=makeQuery(id+"F5.boolean.opBoolean","INTERSECT",EDGE,{"derivedFrom":[makeQuery(id+"F1.opExtrude","SWEPT_FACE",FACE,{"disambiguationData":[OSD([sQuery(id+"F0.wireOp",EDGE,"E119")])]}),makeQuery(id+"F5.opRevolve","SWEPT_FACE",FACE,{"disambiguationData":[OSD([sQuery(id+"F4.wireOp",EDGE,"E149.filletArc")])]})]});
            var Q63;
            Q63=makeQuery(id+"F5.boolean.opBoolean","INTERSECT",EDGE,{"derivedFrom":[makeQuery(id+"F1.opExtrude","SWEPT_FACE",FACE,{"disambiguationData":[OSD([sQuery(id+"F0.wireOp",EDGE,"E121")])]}),makeQuery(id+"F5.opRevolve","SWEPT_FACE",FACE,{"disambiguationData":[OSD([sQuery(id+"F4.wireOp",EDGE,"E149.filletArc")])]})]});
            var Q64;
            Q64=makeQuery(id+"F5.boolean.opBoolean","INTERSECT",EDGE,{"derivedFrom":[makeQuery(id+"F1.opExtrude","SWEPT_FACE",FACE,{"disambiguationData":[OSD([sQuery(id+"F0.wireOp",EDGE,"E113")])]}),makeQuery(id+"F5.opRevolve","SWEPT_FACE",FACE,{"disambiguationData":[OSD([sQuery(id+"F4.wireOp",EDGE,"E149.filletArc")])]})]});
            var Q65;
            Q65=makeQuery(id+"F5.boolean.opBoolean","INTERSECT",EDGE,{"derivedFrom":[makeQuery(id+"F1.opExtrude","SWEPT_FACE",FACE,{"disambiguationData":[OSD([sQuery(id+"F0.wireOp",EDGE,"E129")])]}),makeQuery(id+"F5.opRevolve","SWEPT_FACE",FACE,{"disambiguationData":[OSD([sQuery(id+"F4.wireOp",EDGE,"E149.filletArc")])]})]});
            var Q66;
            Q66=makeQuery(id+"F5.boolean.opBoolean","INTERSECT",EDGE,{"derivedFrom":[makeQuery(id+"F1.opExtrude","SWEPT_FACE",FACE,{"disambiguationData":[OSD([sQuery(id+"F0.wireOp",EDGE,"E137")])]}),makeQuery(id+"F5.opRevolve","SWEPT_FACE",FACE,{"disambiguationData":[OSD([sQuery(id+"F4.wireOp",EDGE,"E149.filletArc")])]})]});
            var Q67;
            Q67=makeQuery(id+"F5.boolean.opBoolean","INTERSECT",EDGE,{"derivedFrom":[makeQuery(id+"F1.opExtrude","SWEPT_FACE",FACE,{"disambiguationData":[OSD([sQuery(id+"F0.wireOp",EDGE,"E127")])]}),makeQuery(id+"F5.opRevolve","SWEPT_FACE",FACE,{"disambiguationData":[OSD([sQuery(id+"F4.wireOp",EDGE,"E149.filletArc")])]})]});
            var Q68;
            Q68=makeQuery(id+"F5.boolean.opBoolean","INTERSECT",EDGE,{"derivedFrom":[makeQuery(id+"F1.opExtrude","SWEPT_FACE",FACE,{"disambiguationData":[OSD([sQuery(id+"F0.wireOp",EDGE,"E135")])]}),makeQuery(id+"F5.opRevolve","SWEPT_FACE",FACE,{"disambiguationData":[OSD([sQuery(id+"F4.wireOp",EDGE,"E149.filletArc")])]})]});
            var Q69;
            Q69=makeQuery(id+"F5.boolean.opBoolean","INTERSECT",EDGE,{"derivedFrom":[makeQuery(id+"F1.opExtrude","SWEPT_FACE",FACE,{"disambiguationData":[OSD([sQuery(id+"F0.wireOp",EDGE,"E7")])]}),makeQuery(id+"F5.opRevolve","SWEPT_FACE",FACE,{"disambiguationData":[OSD([sQuery(id+"F4.wireOp",EDGE,"E149.filletArc")])]})]});
            var Q70;
            Q70=makeQuery(id+"F5.boolean.opBoolean","INTERSECT",EDGE,{"derivedFrom":[makeQuery(id+"F1.opExtrude","SWEPT_FACE",FACE,{"disambiguationData":[OSD([sQuery(id+"F0.wireOp",EDGE,"E143")])]}),makeQuery(id+"F5.opRevolve","SWEPT_FACE",FACE,{"disambiguationData":[OSD([sQuery(id+"F4.wireOp",EDGE,"E149.filletArc")])]})]});
            var Q71;
            Q71=makeQuery(id+"F5.boolean.opBoolean","INTERSECT",EDGE,{"derivedFrom":[makeQuery(id+"F1.opExtrude","SWEPT_FACE",FACE,{"disambiguationData":[OSD([sQuery(id+"F0.wireOp",EDGE,"E17")])]}),makeQuery(id+"F5.opRevolve","SWEPT_FACE",FACE,{"disambiguationData":[OSD([sQuery(id+"F4.wireOp",EDGE,"E149.filletArc")])]})]});
            var Q72;
            Q72=makeQuery(id+"F5.boolean.opBoolean","INTERSECT",EDGE,{"derivedFrom":[makeQuery(id+"F1.opExtrude","SWEPT_FACE",FACE,{"disambiguationData":[OSD([sQuery(id+"F0.wireOp",EDGE,"E9")])]}),makeQuery(id+"F5.opRevolve","SWEPT_FACE",FACE,{"disambiguationData":[OSD([sQuery(id+"F4.wireOp",EDGE,"E149.filletArc")])]})]});
            var Q73;
            Q73=makeQuery(id+"F5.boolean.opBoolean","INTERSECT",EDGE,{"derivedFrom":[makeQuery(id+"F1.opExtrude","SWEPT_FACE",FACE,{"disambiguationData":[OSD([sQuery(id+"F0.wireOp",EDGE,"E1")])]}),makeQuery(id+"F5.opRevolve","SWEPT_FACE",FACE,{"disambiguationData":[OSD([sQuery(id+"F4.wireOp",EDGE,"E149.filletArc")])]})]});
            var Q74;
            Q74=makeQuery(id+"F5.boolean.opBoolean","INTERSECT",EDGE,{"derivedFrom":[makeQuery(id+"F1.opExtrude","SWEPT_FACE",FACE,{"disambiguationData":[OSD([sQuery(id+"F0.wireOp",EDGE,"E124")])]}),makeQuery(id+"F5.opRevolve","SWEPT_FACE",FACE,{"disambiguationData":[OSD([sQuery(id+"F4.wireOp",EDGE,"E147.top")])]})]});
            var Q75;
            Q75=makeQuery(id+"F5.boolean.opBoolean","INTERSECT",EDGE,{"derivedFrom":[makeQuery(id+"F1.opExtrude","SWEPT_FACE",FACE,{"disambiguationData":[OSD([sQuery(id+"F0.wireOp",EDGE,"E132")])]}),makeQuery(id+"F5.opRevolve","SWEPT_FACE",FACE,{"disambiguationData":[OSD([sQuery(id+"F4.wireOp",EDGE,"E147.top")])]})]});
            var Q76;
            Q76=makeQuery(id+"F5.boolean.opBoolean","INTERSECT",EDGE,{"derivedFrom":[makeQuery(id+"F1.opExtrude","SWEPT_FACE",FACE,{"disambiguationData":[OSD([sQuery(id+"F0.wireOp",EDGE,"E124")])]}),makeQuery(id+"F5.opRevolve","SWEPT_FACE",FACE,{"disambiguationData":[OSD([sQuery(id+"F4.wireOp",EDGE,"E147.bottom")])]})]});
            var Q77;
            Q77=makeQuery(id+"F5.boolean.opBoolean","INTERSECT",EDGE,{"derivedFrom":[makeQuery(id+"F1.opExtrude","SWEPT_FACE",FACE,{"disambiguationData":[OSD([sQuery(id+"F0.wireOp",EDGE,"E116")])]}),makeQuery(id+"F5.opRevolve","SWEPT_FACE",FACE,{"disambiguationData":[OSD([sQuery(id+"F4.wireOp",EDGE,"E147.top")])]})]});
            var Q78;
            Q78=makeQuery(id+"F5.boolean.opBoolean","INTERSECT",EDGE,{"derivedFrom":[makeQuery(id+"F1.opExtrude","SWEPT_FACE",FACE,{"disambiguationData":[OSD([sQuery(id+"F0.wireOp",EDGE,"E116")])]}),makeQuery(id+"F5.opRevolve","SWEPT_FACE",FACE,{"disambiguationData":[OSD([sQuery(id+"F4.wireOp",EDGE,"E147.bottom")])]})]});
            var Q79;
            Q79=makeQuery(id+"F5.boolean.opBoolean","INTERSECT",EDGE,{"derivedFrom":[makeQuery(id+"F1.opExtrude","SWEPT_FACE",FACE,{"disambiguationData":[OSD([sQuery(id+"F0.wireOp",EDGE,"E108")])]}),makeQuery(id+"F5.opRevolve","SWEPT_FACE",FACE,{"disambiguationData":[OSD([sQuery(id+"F4.wireOp",EDGE,"E147.top")])]})]});
            var Q80;
            Q80=makeQuery(id+"F5.boolean.opBoolean","INTERSECT",EDGE,{"derivedFrom":[makeQuery(id+"F1.opExtrude","SWEPT_FACE",FACE,{"disambiguationData":[OSD([sQuery(id+"F0.wireOp",EDGE,"E108")])]}),makeQuery(id+"F5.opRevolve","SWEPT_FACE",FACE,{"disambiguationData":[OSD([sQuery(id+"F4.wireOp",EDGE,"E147.bottom")])]})]});
            var Q81;
            Q81=makeQuery(id+"F1.opExtrude","CAP_EDGE",EDGE,{"disambiguationData":[OSD([sQuery(id+"F0.wireOp",EDGE,"E72")])],"isStart":false});
            var Q82;
            Q82=makeQuery(id+"F1.opExtrude","CAP_EDGE",EDGE,{"disambiguationData":[OSD([sQuery(id+"F0.wireOp",EDGE,"E64")])],"isStart":false});
            var Q83;
            Q83=makeQuery(id+"F1.opExtrude","CAP_EDGE",EDGE,{"disambiguationData":[OSD([sQuery(id+"F0.wireOp",EDGE,"E56")])],"isStart":false});
            var Q84;
            Q84=makeQuery(id+"F5.boolean.opBoolean","INTERSECT",EDGE,{"derivedFrom":[makeQuery(id+"F1.opExtrude","SWEPT_FACE",FACE,{"disambiguationData":[OSD([sQuery(id+"F0.wireOp",EDGE,"E55")])]}),makeQuery(id+"F5.opRevolve","SWEPT_FACE",FACE,{"disambiguationData":[OSD([sQuery(id+"F4.wireOp",EDGE,"E149.filletArc")])]})]});
            var Q85;
            Q85=makeQuery(id+"F5.boolean.opBoolean","INTERSECT",EDGE,{"derivedFrom":[makeQuery(id+"F1.opExtrude","SWEPT_FACE",FACE,{"disambiguationData":[OSD([sQuery(id+"F0.wireOp",EDGE,"E47")])]}),makeQuery(id+"F5.opRevolve","SWEPT_FACE",FACE,{"disambiguationData":[OSD([sQuery(id+"F4.wireOp",EDGE,"E149.filletArc")])]})]});
            var Q86;
            Q86=makeQuery(id+"F5.boolean.opBoolean","INTERSECT",EDGE,{"derivedFrom":[makeQuery(id+"F1.opExtrude","SWEPT_FACE",FACE,{"disambiguationData":[OSD([sQuery(id+"F0.wireOp",EDGE,"E63")])]}),makeQuery(id+"F5.opRevolve","SWEPT_FACE",FACE,{"disambiguationData":[OSD([sQuery(id+"F4.wireOp",EDGE,"E149.filletArc")])]})]});
            var Q87;
            Q87=makeQuery(id+"F5.boolean.opBoolean","INTERSECT",EDGE,{"derivedFrom":[makeQuery(id+"F1.opExtrude","SWEPT_FACE",FACE,{"disambiguationData":[OSD([sQuery(id+"F0.wireOp",EDGE,"E71")])]}),makeQuery(id+"F5.opRevolve","SWEPT_FACE",FACE,{"disambiguationData":[OSD([sQuery(id+"F4.wireOp",EDGE,"E149.filletArc")])]})]});
            var Q88;
            Q88=makeQuery(id+"F1.opExtrude","CAP_EDGE",EDGE,{"disambiguationData":[OSD([sQuery(id+"F0.wireOp",EDGE,"E16")])],"isStart":false});
            var Q89;
            Q89=makeQuery(id+"F1.opExtrude","CAP_EDGE",EDGE,{"disambiguationData":[OSD([sQuery(id+"F0.wireOp",EDGE,"E24")])],"isStart":false});
            var Q90;
            Q90=makeQuery(id+"F1.opExtrude","CAP_EDGE",EDGE,{"disambiguationData":[OSD([sQuery(id+"F0.wireOp",EDGE,"E32")])],"isStart":false});
            var Q91;
            Q91=makeQuery(id+"F1.opExtrude","CAP_EDGE",EDGE,{"disambiguationData":[OSD([sQuery(id+"F0.wireOp",EDGE,"E40")])],"isStart":false});
            var Q92;
            Q92=makeQuery(id+"F1.opExtrude","CAP_EDGE",EDGE,{"disambiguationData":[OSD([sQuery(id+"F0.wireOp",EDGE,"E48")])],"isStart":false});
            var Q93;
            Q93=makeQuery(id+"F1.opExtrude","CAP_EDGE",EDGE,{"disambiguationData":[OSD([sQuery(id+"F0.wireOp",EDGE,"E80")])],"isStart":false});
            var Q94;
            Q94=makeQuery(id+"F1.opExtrude","CAP_EDGE",EDGE,{"disambiguationData":[OSD([sQuery(id+"F0.wireOp",EDGE,"E88")])],"isStart":false});
            var Q95;
            Q95=makeQuery(id+"F1.opExtrude","CAP_EDGE",EDGE,{"disambiguationData":[OSD([sQuery(id+"F0.wireOp",EDGE,"E96")])],"isStart":false});
            var Q96;
            Q96=makeQuery(id+"F1.opExtrude","CAP_EDGE",EDGE,{"disambiguationData":[OSD([sQuery(id+"F0.wireOp",EDGE,"E104")])],"isStart":false});
            var Q97;
            Q97=makeQuery(id+"F1.opExtrude","CAP_EDGE",EDGE,{"disambiguationData":[OSD([sQuery(id+"F0.wireOp",EDGE,"E112")])],"isStart":false});
            var Q98;
            Q98=makeQuery(id+"F1.opExtrude","CAP_EDGE",EDGE,{"disambiguationData":[OSD([sQuery(id+"F0.wireOp",EDGE,"E120")])],"isStart":false});
            var Q99;
            Q99=makeQuery(id+"F1.opExtrude","CAP_EDGE",EDGE,{"disambiguationData":[OSD([sQuery(id+"F0.wireOp",EDGE,"E128")])],"isStart":false});
            var Q100;
            Q100=makeQuery(id+"F1.opExtrude","CAP_EDGE",EDGE,{"disambiguationData":[OSD([sQuery(id+"F0.wireOp",EDGE,"E136")])],"isStart":false});
            var Q101;
            Q101=makeQuery(id+"F1.opExtrude","CAP_EDGE",EDGE,{"disambiguationData":[OSD([sQuery(id+"F0.wireOp",EDGE,"E144")])],"isStart":false});
            var Q102;
            Q102=makeQuery(id+"F1.opExtrude","CAP_EDGE",EDGE,{"disambiguationData":[OSD([sQuery(id+"F0.wireOp",EDGE,"E8")])],"isStart":false});
            var Q103;
            Q103=makeQuery(id+"F1.opExtrude","CAP_EDGE",EDGE,{"disambiguationData":[OSD([sQuery(id+"F0.wireOp",EDGE,"E82")])],"isStart":true});
            var Q104;
            Q104=makeQuery(id+"F1.opExtrude","CAP_EDGE",EDGE,{"disambiguationData":[OSD([sQuery(id+"F0.wireOp",EDGE,"E90")])],"isStart":true});
            var Q105;
            Q105=makeQuery(id+"F1.opExtrude","CAP_EDGE",EDGE,{"disambiguationData":[OSD([sQuery(id+"F0.wireOp",EDGE,"E98")])],"isStart":true});
            var Q106;
            Q106=makeQuery(id+"F1.opExtrude","CAP_EDGE",EDGE,{"disambiguationData":[OSD([sQuery(id+"F0.wireOp",EDGE,"E106")])],"isStart":true});
            var Q107;
            Q107=makeQuery(id+"F1.opExtrude","CAP_EDGE",EDGE,{"disambiguationData":[OSD([sQuery(id+"F0.wireOp",EDGE,"E114")])],"isStart":true});
            var Q108;
            Q108=makeQuery(id+"F1.opExtrude","CAP_EDGE",EDGE,{"disambiguationData":[OSD([sQuery(id+"F0.wireOp",EDGE,"E122")])],"isStart":true});
            var Q109;
            Q109=makeQuery(id+"F1.opExtrude","CAP_EDGE",EDGE,{"disambiguationData":[OSD([sQuery(id+"F0.wireOp",EDGE,"E130")])],"isStart":true});
            var Q110;
            Q110=makeQuery(id+"F1.opExtrude","CAP_EDGE",EDGE,{"disambiguationData":[OSD([sQuery(id+"F0.wireOp",EDGE,"E138")])],"isStart":true});
            var Q111;
            Q111=makeQuery(id+"F1.opExtrude","CAP_EDGE",EDGE,{"disambiguationData":[OSD([sQuery(id+"F0.wireOp",EDGE,"E2")])],"isStart":true});
            var Q112;
            Q112=makeQuery(id+"F1.opExtrude","CAP_EDGE",EDGE,{"disambiguationData":[OSD([sQuery(id+"F0.wireOp",EDGE,"E10")])],"isStart":true});
            var Q113;
            Q113=makeQuery(id+"F1.opExtrude","CAP_EDGE",EDGE,{"disambiguationData":[OSD([sQuery(id+"F0.wireOp",EDGE,"E18")])],"isStart":true});
            var Q114;
            Q114=makeQuery(id+"F1.opExtrude","CAP_EDGE",EDGE,{"disambiguationData":[OSD([sQuery(id+"F0.wireOp",EDGE,"E26")])],"isStart":true});
            var Q115;
            Q115=makeQuery(id+"F1.opExtrude","CAP_EDGE",EDGE,{"disambiguationData":[OSD([sQuery(id+"F0.wireOp",EDGE,"E34")])],"isStart":true});
            var Q116;
            Q116=makeQuery(id+"F1.opExtrude","CAP_EDGE",EDGE,{"disambiguationData":[OSD([sQuery(id+"F0.wireOp",EDGE,"E22")])],"isStart":true});
            var Q117;
            Q117=makeQuery(id+"F1.opExtrude","CAP_EDGE",EDGE,{"disambiguationData":[OSD([sQuery(id+"F0.wireOp",EDGE,"E30")])],"isStart":true});
            var Q118;
            Q118=makeQuery(id+"F1.opExtrude","CAP_EDGE",EDGE,{"disambiguationData":[OSD([sQuery(id+"F0.wireOp",EDGE,"E38")])],"isStart":true});
            var Q119;
            Q119=makeQuery(id+"F1.opExtrude","CAP_EDGE",EDGE,{"disambiguationData":[OSD([sQuery(id+"F0.wireOp",EDGE,"E46")])],"isStart":true});
            var Q120;
            Q120=makeQuery(id+"F1.opExtrude","CAP_EDGE",EDGE,{"disambiguationData":[OSD([sQuery(id+"F0.wireOp",EDGE,"E54")])],"isStart":true});
            var Q121;
            Q121=makeQuery(id+"F1.opExtrude","CAP_EDGE",EDGE,{"disambiguationData":[OSD([sQuery(id+"F0.wireOp",EDGE,"E62")])],"isStart":true});
            var Q122;
            Q122=makeQuery(id+"F1.opExtrude","CAP_EDGE",EDGE,{"disambiguationData":[OSD([sQuery(id+"F0.wireOp",EDGE,"E70")])],"isStart":true});
            var Q123;
            Q123=makeQuery(id+"F1.opExtrude","CAP_EDGE",EDGE,{"disambiguationData":[OSD([sQuery(id+"F0.wireOp",EDGE,"E78")])],"isStart":true});
            var Q124;
            Q124=makeQuery(id+"F1.opExtrude","CAP_EDGE",EDGE,{"disambiguationData":[OSD([sQuery(id+"F0.wireOp",EDGE,"E86")])],"isStart":true});
            var Q125;
            Q125=makeQuery(id+"F1.opExtrude","CAP_EDGE",EDGE,{"disambiguationData":[OSD([sQuery(id+"F0.wireOp",EDGE,"E94")])],"isStart":true});
            var Q126;
            Q126=makeQuery(id+"F1.opExtrude","CAP_EDGE",EDGE,{"disambiguationData":[OSD([sQuery(id+"F0.wireOp",EDGE,"E102")])],"isStart":true});
            var Q127;
            Q127=makeQuery(id+"F1.opExtrude","CAP_EDGE",EDGE,{"disambiguationData":[OSD([sQuery(id+"F0.wireOp",EDGE,"E110")])],"isStart":true});
            var Q128;
            Q128=makeQuery(id+"F1.opExtrude","CAP_EDGE",EDGE,{"disambiguationData":[OSD([sQuery(id+"F0.wireOp",EDGE,"E118")])],"isStart":true});
            var Q129;
            Q129=makeQuery(id+"F1.opExtrude","CAP_EDGE",EDGE,{"disambiguationData":[OSD([sQuery(id+"F0.wireOp",EDGE,"E126")])],"isStart":true});
            var Q130;
            Q130=makeQuery(id+"F1.opExtrude","CAP_EDGE",EDGE,{"disambiguationData":[OSD([sQuery(id+"F0.wireOp",EDGE,"E134")])],"isStart":true});
            var Q131;
            Q131=makeQuery(id+"F1.opExtrude","CAP_EDGE",EDGE,{"disambiguationData":[OSD([sQuery(id+"F0.wireOp",EDGE,"E142")])],"isStart":true});
            var Q132;
            Q132=makeQuery(id+"F1.opExtrude","CAP_EDGE",EDGE,{"disambiguationData":[OSD([sQuery(id+"F0.wireOp",EDGE,"E6")])],"isStart":true});
            var Q133;
            Q133=makeQuery(id+"F1.opExtrude","CAP_EDGE",EDGE,{"disambiguationData":[OSD([sQuery(id+"F0.wireOp",EDGE,"E74")])],"isStart":true});
            var Q134;
            Q134=makeQuery(id+"F1.opExtrude","CAP_EDGE",EDGE,{"disambiguationData":[OSD([sQuery(id+"F0.wireOp",EDGE,"E66")])],"isStart":true});
            var Q135;
            Q135=makeQuery(id+"F1.opExtrude","CAP_EDGE",EDGE,{"disambiguationData":[OSD([sQuery(id+"F0.wireOp",EDGE,"E42")])],"isStart":true});
            var Q136;
            Q136=makeQuery(id+"F1.opExtrude","CAP_EDGE",EDGE,{"disambiguationData":[OSD([sQuery(id+"F0.wireOp",EDGE,"E14")])],"isStart":true});
            var Q137;
            Q137=makeQuery(id+"F1.opExtrude","CAP_EDGE",EDGE,{"disambiguationData":[OSD([sQuery(id+"F0.wireOp",EDGE,"E28")])],"isStart":true});
            var Q138;
            Q138=makeQuery(id+"F1.opExtrude","CAP_EDGE",EDGE,{"disambiguationData":[OSD([sQuery(id+"F0.wireOp",EDGE,"E20")])],"isStart":true});
            var Q139;
            Q139=makeQuery(id+"F1.opExtrude","CAP_EDGE",EDGE,{"disambiguationData":[OSD([sQuery(id+"F0.wireOp",EDGE,"E12")])],"isStart":true});
            var Q140;
            Q140=makeQuery(id+"F1.opExtrude","CAP_EDGE",EDGE,{"disambiguationData":[OSD([sQuery(id+"F0.wireOp",EDGE,"E4")])],"isStart":true});
            var Q141;
            Q141=makeQuery(id+"F1.opExtrude","CAP_EDGE",EDGE,{"disambiguationData":[OSD([sQuery(id+"F0.wireOp",EDGE,"E36")])],"isStart":true});
            var Q142;
            Q142=makeQuery(id+"F1.opExtrude","CAP_EDGE",EDGE,{"disambiguationData":[OSD([sQuery(id+"F0.wireOp",EDGE,"E44")])],"isStart":true});
            var Q143;
            Q143=makeQuery(id+"F1.opExtrude","CAP_EDGE",EDGE,{"disambiguationData":[OSD([sQuery(id+"F0.wireOp",EDGE,"E52")])],"isStart":true});
            var Q144;
            Q144=makeQuery(id+"F1.opExtrude","CAP_EDGE",EDGE,{"disambiguationData":[OSD([sQuery(id+"F0.wireOp",EDGE,"E60")])],"isStart":true});
            var Q145;
            Q145=makeQuery(id+"F1.opExtrude","CAP_EDGE",EDGE,{"disambiguationData":[OSD([sQuery(id+"F0.wireOp",EDGE,"E68")])],"isStart":true});
            var Q146;
            Q146=makeQuery(id+"F1.opExtrude","CAP_EDGE",EDGE,{"disambiguationData":[OSD([sQuery(id+"F0.wireOp",EDGE,"E76")])],"isStart":true});
            var Q147;
            Q147=makeQuery(id+"F1.opExtrude","CAP_EDGE",EDGE,{"disambiguationData":[OSD([sQuery(id+"F0.wireOp",EDGE,"E84")])],"isStart":true});
            var Q148;
            Q148=makeQuery(id+"F1.opExtrude","CAP_EDGE",EDGE,{"disambiguationData":[OSD([sQuery(id+"F0.wireOp",EDGE,"E92")])],"isStart":true});
            var Q149;
            Q149=makeQuery(id+"F1.opExtrude","CAP_EDGE",EDGE,{"disambiguationData":[OSD([sQuery(id+"F0.wireOp",EDGE,"E100")])],"isStart":true});
            var Q150;
            Q150=makeQuery(id+"F1.opExtrude","CAP_EDGE",EDGE,{"disambiguationData":[OSD([sQuery(id+"F0.wireOp",EDGE,"E108")])],"isStart":true});
            var Q151;
            Q151=makeQuery(id+"F1.opExtrude","CAP_EDGE",EDGE,{"disambiguationData":[OSD([sQuery(id+"F0.wireOp",EDGE,"E116")])],"isStart":true});
            var Q152;
            Q152=makeQuery(id+"F1.opExtrude","CAP_EDGE",EDGE,{"disambiguationData":[OSD([sQuery(id+"F0.wireOp",EDGE,"E124")])],"isStart":true});
            var Q153;
            Q153=makeQuery(id+"F1.opExtrude","CAP_EDGE",EDGE,{"disambiguationData":[OSD([sQuery(id+"F0.wireOp",EDGE,"E132")])],"isStart":true});
            var Q154;
            Q154=makeQuery(id+"F1.opExtrude","CAP_EDGE",EDGE,{"disambiguationData":[OSD([sQuery(id+"F0.wireOp",EDGE,"E140")])],"isStart":true});
            var Q155;
            Q155=makeQuery(id+"F1.opExtrude","CAP_EDGE",EDGE,{"disambiguationData":[OSD([sQuery(id+"F0.wireOp",EDGE,"E58")])],"isStart":true});
            var Q156;
            Q156=makeQuery(id+"F1.opExtrude","CAP_EDGE",EDGE,{"disambiguationData":[OSD([sQuery(id+"F0.wireOp",EDGE,"E50")])],"isStart":true});
            var Q157;
            Q157=makeQuery(id+"F1.opExtrude","CAP_EDGE",EDGE,{"disambiguationData":[OSD([sQuery(id+"F0.wireOp",EDGE,"E56")])],"isStart":true});
            var Q158;
            Q158=makeQuery(id+"F1.opExtrude","CAP_EDGE",EDGE,{"disambiguationData":[OSD([sQuery(id+"F0.wireOp",EDGE,"E64")])],"isStart":true});
            var Q159;
            Q159=makeQuery(id+"F1.opExtrude","CAP_EDGE",EDGE,{"disambiguationData":[OSD([sQuery(id+"F0.wireOp",EDGE,"E72")])],"isStart":true});
            var Q160;
            Q160=makeQuery(id+"F1.opExtrude","CAP_EDGE",EDGE,{"disambiguationData":[OSD([sQuery(id+"F0.wireOp",EDGE,"E80")])],"isStart":true});
            var Q161;
            Q161=makeQuery(id+"F1.opExtrude","CAP_EDGE",EDGE,{"disambiguationData":[OSD([sQuery(id+"F0.wireOp",EDGE,"E88")])],"isStart":true});
            var Q162;
            Q162=makeQuery(id+"F1.opExtrude","CAP_EDGE",EDGE,{"disambiguationData":[OSD([sQuery(id+"F0.wireOp",EDGE,"E96")])],"isStart":true});
            var Q163;
            Q163=makeQuery(id+"F1.opExtrude","CAP_EDGE",EDGE,{"disambiguationData":[OSD([sQuery(id+"F0.wireOp",EDGE,"E104")])],"isStart":true});
            var Q164;
            Q164=makeQuery(id+"F1.opExtrude","CAP_EDGE",EDGE,{"disambiguationData":[OSD([sQuery(id+"F0.wireOp",EDGE,"E112")])],"isStart":true});
            var Q165;
            Q165=makeQuery(id+"F1.opExtrude","CAP_EDGE",EDGE,{"disambiguationData":[OSD([sQuery(id+"F0.wireOp",EDGE,"E120")])],"isStart":true});
            var Q166;
            Q166=makeQuery(id+"F1.opExtrude","CAP_EDGE",EDGE,{"disambiguationData":[OSD([sQuery(id+"F0.wireOp",EDGE,"E128")])],"isStart":true});
            var Q167;
            Q167=makeQuery(id+"F1.opExtrude","CAP_EDGE",EDGE,{"disambiguationData":[OSD([sQuery(id+"F0.wireOp",EDGE,"E136")])],"isStart":true});
            var Q168;
            Q168=makeQuery(id+"F1.opExtrude","CAP_EDGE",EDGE,{"disambiguationData":[OSD([sQuery(id+"F0.wireOp",EDGE,"E144")])],"isStart":true});
            var Q169;
            Q169=makeQuery(id+"F1.opExtrude","CAP_EDGE",EDGE,{"disambiguationData":[OSD([sQuery(id+"F0.wireOp",EDGE,"E40")])],"isStart":true});
            var Q170;
            Q170=makeQuery(id+"F1.opExtrude","CAP_EDGE",EDGE,{"disambiguationData":[OSD([sQuery(id+"F0.wireOp",EDGE,"E48")])],"isStart":true});
            var Q171;
            Q171=makeQuery(id+"F1.opExtrude","CAP_EDGE",EDGE,{"disambiguationData":[OSD([sQuery(id+"F0.wireOp",EDGE,"E32")])],"isStart":true});
            var Q172;
            Q172=makeQuery(id+"F1.opExtrude","CAP_EDGE",EDGE,{"disambiguationData":[OSD([sQuery(id+"F0.wireOp",EDGE,"E24")])],"isStart":true});
            var Q173;
            Q173=makeQuery(id+"F1.opExtrude","CAP_EDGE",EDGE,{"disambiguationData":[OSD([sQuery(id+"F0.wireOp",EDGE,"E16")])],"isStart":true});
            var Q174;
            Q174=makeQuery(id+"F1.opExtrude","CAP_EDGE",EDGE,{"disambiguationData":[OSD([sQuery(id+"F0.wireOp",EDGE,"E8")])],"isStart":true});
            var Q175;
            Q175=makeQuery(id+"F5.boolean.opBoolean","INTERSECT",EDGE,{"derivedFrom":[makeQuery(id+"F1.opExtrude","SWEPT_FACE",FACE,{"disambiguationData":[OSD([sQuery(id+"F0.wireOp",EDGE,"E74")])]}),makeQuery(id+"F5.opRevolve","SWEPT_FACE",FACE,{"disambiguationData":[OSD([sQuery(id+"F4.wireOp",EDGE,"E147.bottom")])]})]});
            var Q176;
            Q176=makeQuery(id+"F5.boolean.opBoolean","INTERSECT",EDGE,{"derivedFrom":[makeQuery(id+"F1.opExtrude","SWEPT_FACE",FACE,{"disambiguationData":[OSD([sQuery(id+"F0.wireOp",EDGE,"E66")])]}),makeQuery(id+"F5.opRevolve","SWEPT_FACE",FACE,{"disambiguationData":[OSD([sQuery(id+"F4.wireOp",EDGE,"E147.bottom")])]})]});
            var Q177;
            Q177=makeQuery(id+"F5.boolean.opBoolean","INTERSECT",EDGE,{"derivedFrom":[makeQuery(id+"F1.opExtrude","SWEPT_FACE",FACE,{"disambiguationData":[OSD([sQuery(id+"F0.wireOp",EDGE,"E58")])]}),makeQuery(id+"F5.opRevolve","SWEPT_FACE",FACE,{"disambiguationData":[OSD([sQuery(id+"F4.wireOp",EDGE,"E147.bottom")])]})]});
            var Q178;
            Q178=makeQuery(id+"F5.boolean.opBoolean","INTERSECT",EDGE,{"derivedFrom":[makeQuery(id+"F1.opExtrude","SWEPT_FACE",FACE,{"disambiguationData":[OSD([sQuery(id+"F0.wireOp",EDGE,"E50")])]}),makeQuery(id+"F5.opRevolve","SWEPT_FACE",FACE,{"disambiguationData":[OSD([sQuery(id+"F4.wireOp",EDGE,"E147.bottom")])]})]});
            var Q179;
            Q179=makeQuery(id+"F5.boolean.opBoolean","INTERSECT",EDGE,{"derivedFrom":[makeQuery(id+"F1.opExtrude","SWEPT_FACE",FACE,{"disambiguationData":[OSD([sQuery(id+"F0.wireOp",EDGE,"E34")])]}),makeQuery(id+"F5.opRevolve","SWEPT_FACE",FACE,{"disambiguationData":[OSD([sQuery(id+"F4.wireOp",EDGE,"E147.bottom")])]})]});
            var Q180;
            Q180=makeQuery(id+"F5.boolean.opBoolean","INTERSECT",EDGE,{"derivedFrom":[makeQuery(id+"F1.opExtrude","SWEPT_FACE",FACE,{"disambiguationData":[OSD([sQuery(id+"F0.wireOp",EDGE,"E26")])]}),makeQuery(id+"F5.opRevolve","SWEPT_FACE",FACE,{"disambiguationData":[OSD([sQuery(id+"F4.wireOp",EDGE,"E147.bottom")])]})]});
            var Q181;
            Q181=makeQuery(id+"F5.boolean.opBoolean","INTERSECT",EDGE,{"derivedFrom":[makeQuery(id+"F1.opExtrude","SWEPT_FACE",FACE,{"disambiguationData":[OSD([sQuery(id+"F0.wireOp",EDGE,"E38")])]}),makeQuery(id+"F5.opRevolve","SWEPT_FACE",FACE,{"disambiguationData":[OSD([sQuery(id+"F4.wireOp",EDGE,"E147.bottom")])]})]});
            var Q182;
            Q182=makeQuery(id+"F5.boolean.opBoolean","INTERSECT",EDGE,{"derivedFrom":[makeQuery(id+"F1.opExtrude","SWEPT_FACE",FACE,{"disambiguationData":[OSD([sQuery(id+"F0.wireOp",EDGE,"E38")])]}),makeQuery(id+"F5.opRevolve","SWEPT_FACE",FACE,{"disambiguationData":[OSD([sQuery(id+"F4.wireOp",EDGE,"E147.top")])]})]});
            var Q183;
            Q183=makeQuery(id+"F5.boolean.opBoolean","INTERSECT",EDGE,{"derivedFrom":[makeQuery(id+"F1.opExtrude","SWEPT_FACE",FACE,{"disambiguationData":[OSD([sQuery(id+"F0.wireOp",EDGE,"E42")])]}),makeQuery(id+"F5.opRevolve","SWEPT_FACE",FACE,{"disambiguationData":[OSD([sQuery(id+"F4.wireOp",EDGE,"E147.top")])]})]});
            var Q184;
            Q184=makeQuery(id+"F5.boolean.opBoolean","INTERSECT",EDGE,{"derivedFrom":[makeQuery(id+"F1.opExtrude","SWEPT_FACE",FACE,{"disambiguationData":[OSD([sQuery(id+"F0.wireOp",EDGE,"E22")])]}),makeQuery(id+"F5.opRevolve","SWEPT_FACE",FACE,{"disambiguationData":[OSD([sQuery(id+"F4.wireOp",EDGE,"E147.top")])]})]});
            var Q185;
            Q185=makeQuery(id+"F5.boolean.opBoolean","INTERSECT",EDGE,{"derivedFrom":[makeQuery(id+"F1.opExtrude","SWEPT_FACE",FACE,{"disambiguationData":[OSD([sQuery(id+"F0.wireOp",EDGE,"E22")])]}),makeQuery(id+"F5.opRevolve","SWEPT_FACE",FACE,{"disambiguationData":[OSD([sQuery(id+"F4.wireOp",EDGE,"E147.bottom")])]})]});
            var Q186;
            Q186=makeQuery(id+"F5.boolean.opBoolean","INTERSECT",EDGE,{"derivedFrom":[makeQuery(id+"F1.opExtrude","SWEPT_FACE",FACE,{"disambiguationData":[OSD([sQuery(id+"F0.wireOp",EDGE,"E14")])]}),makeQuery(id+"F5.opRevolve","SWEPT_FACE",FACE,{"disambiguationData":[OSD([sQuery(id+"F4.wireOp",EDGE,"E147.top")])]})]});
            var Q187;
            Q187=makeQuery(id+"F5.boolean.opBoolean","INTERSECT",EDGE,{"derivedFrom":[makeQuery(id+"F1.opExtrude","SWEPT_FACE",FACE,{"disambiguationData":[OSD([sQuery(id+"F0.wireOp",EDGE,"E14")])]}),makeQuery(id+"F5.opRevolve","SWEPT_FACE",FACE,{"disambiguationData":[OSD([sQuery(id+"F4.wireOp",EDGE,"E147.bottom")])]})]});
            var Q188;
            Q188=makeQuery(id+"F5.boolean.opBoolean","INTERSECT",EDGE,{"derivedFrom":[makeQuery(id+"F1.opExtrude","SWEPT_FACE",FACE,{"disambiguationData":[OSD([sQuery(id+"F0.wireOp",EDGE,"E12")])]}),makeQuery(id+"F5.opRevolve","SWEPT_FACE",FACE,{"disambiguationData":[OSD([sQuery(id+"F4.wireOp",EDGE,"E147.top")])]})]});
            var Q189;
            Q189=makeQuery(id+"F5.boolean.opBoolean","INTERSECT",EDGE,{"derivedFrom":[makeQuery(id+"F1.opExtrude","SWEPT_FACE",FACE,{"disambiguationData":[OSD([sQuery(id+"F0.wireOp",EDGE,"E12")])]}),makeQuery(id+"F5.opRevolve","SWEPT_FACE",FACE,{"disambiguationData":[OSD([sQuery(id+"F4.wireOp",EDGE,"E147.bottom")])]})]});
            var Q190;
            Q190=makeQuery(id+"F5.boolean.opBoolean","INTERSECT",EDGE,{"derivedFrom":[makeQuery(id+"F1.opExtrude","SWEPT_FACE",FACE,{"disambiguationData":[OSD([sQuery(id+"F0.wireOp",EDGE,"E4")])]}),makeQuery(id+"F5.opRevolve","SWEPT_FACE",FACE,{"disambiguationData":[OSD([sQuery(id+"F4.wireOp",EDGE,"E147.top")])]})]});
            var Q191;
            Q191=makeQuery(id+"F5.boolean.opBoolean","INTERSECT",EDGE,{"derivedFrom":[makeQuery(id+"F1.opExtrude","SWEPT_FACE",FACE,{"disambiguationData":[OSD([sQuery(id+"F0.wireOp",EDGE,"E4")])]}),makeQuery(id+"F5.opRevolve","SWEPT_FACE",FACE,{"disambiguationData":[OSD([sQuery(id+"F4.wireOp",EDGE,"E147.bottom")])]})]});
            var Q192;
            Q192=makeQuery(id+"F5.boolean.opBoolean","INTERSECT",EDGE,{"derivedFrom":[makeQuery(id+"F1.opExtrude","SWEPT_FACE",FACE,{"disambiguationData":[OSD([sQuery(id+"F0.wireOp",EDGE,"E140")])]}),makeQuery(id+"F5.opRevolve","SWEPT_FACE",FACE,{"disambiguationData":[OSD([sQuery(id+"F4.wireOp",EDGE,"E147.top")])]})]});
            var Q193;
            Q193=makeQuery(id+"F5.boolean.opBoolean","INTERSECT",EDGE,{"derivedFrom":[makeQuery(id+"F1.opExtrude","SWEPT_FACE",FACE,{"disambiguationData":[OSD([sQuery(id+"F0.wireOp",EDGE,"E140")])]}),makeQuery(id+"F5.opRevolve","SWEPT_FACE",FACE,{"disambiguationData":[OSD([sQuery(id+"F4.wireOp",EDGE,"E147.bottom")])]})]});
            var Q194;
            Q194=makeQuery(id+"F5.boolean.opBoolean","INTERSECT",EDGE,{"derivedFrom":[makeQuery(id+"F1.opExtrude","SWEPT_FACE",FACE,{"disambiguationData":[OSD([sQuery(id+"F0.wireOp",EDGE,"E92")])]}),makeQuery(id+"F5.opRevolve","SWEPT_FACE",FACE,{"disambiguationData":[OSD([sQuery(id+"F4.wireOp",EDGE,"E147.top")])]})]});
            var Q195;
            Q195=makeQuery(id+"F5.boolean.opBoolean","INTERSECT",EDGE,{"derivedFrom":[makeQuery(id+"F1.opExtrude","SWEPT_FACE",FACE,{"disambiguationData":[OSD([sQuery(id+"F0.wireOp",EDGE,"E92")])]}),makeQuery(id+"F5.opRevolve","SWEPT_FACE",FACE,{"disambiguationData":[OSD([sQuery(id+"F4.wireOp",EDGE,"E147.bottom")])]})]});
            var Q196;
            Q196=makeQuery(id+"F5.boolean.opBoolean","INTERSECT",EDGE,{"derivedFrom":[makeQuery(id+"F1.opExtrude","SWEPT_FACE",FACE,{"disambiguationData":[OSD([sQuery(id+"F0.wireOp",EDGE,"E100")])]}),makeQuery(id+"F5.opRevolve","SWEPT_FACE",FACE,{"disambiguationData":[OSD([sQuery(id+"F4.wireOp",EDGE,"E147.bottom")])]})]});
            var Q197;
            Q197=makeQuery(id+"F5.boolean.opBoolean","INTERSECT",EDGE,{"derivedFrom":[makeQuery(id+"F1.opExtrude","SWEPT_FACE",FACE,{"disambiguationData":[OSD([sQuery(id+"F0.wireOp",EDGE,"E100")])]}),makeQuery(id+"F5.opRevolve","SWEPT_FACE",FACE,{"disambiguationData":[OSD([sQuery(id+"F4.wireOp",EDGE,"E147.top")])]})]});
            var Q198;
            Q198=makeQuery(id+"F5.boolean.opBoolean","INTERSECT",EDGE,{"derivedFrom":[makeQuery(id+"F1.opExtrude","SWEPT_FACE",FACE,{"disambiguationData":[OSD([sQuery(id+"F0.wireOp",EDGE,"E84")])]}),makeQuery(id+"F5.opRevolve","SWEPT_FACE",FACE,{"disambiguationData":[OSD([sQuery(id+"F4.wireOp",EDGE,"E147.bottom")])]})]});
            var Q199;
            Q199=makeQuery(id+"F5.boolean.opBoolean","INTERSECT",EDGE,{"derivedFrom":[makeQuery(id+"F1.opExtrude","SWEPT_FACE",FACE,{"disambiguationData":[OSD([sQuery(id+"F0.wireOp",EDGE,"E84")])]}),makeQuery(id+"F5.opRevolve","SWEPT_FACE",FACE,{"disambiguationData":[OSD([sQuery(id+"F4.wireOp",EDGE,"E147.top")])]})]});
            var Q200;
            Q200=makeQuery(id+"F5.boolean.opBoolean","INTERSECT",EDGE,{"derivedFrom":[makeQuery(id+"F1.opExtrude","SWEPT_FACE",FACE,{"disambiguationData":[OSD([sQuery(id+"F0.wireOp",EDGE,"E76")])]}),makeQuery(id+"F5.opRevolve","SWEPT_FACE",FACE,{"disambiguationData":[OSD([sQuery(id+"F4.wireOp",EDGE,"E147.top")])]})]});
            var Q201;
            Q201=makeQuery(id+"F5.boolean.opBoolean","INTERSECT",EDGE,{"derivedFrom":[makeQuery(id+"F1.opExtrude","SWEPT_FACE",FACE,{"disambiguationData":[OSD([sQuery(id+"F0.wireOp",EDGE,"E76")])]}),makeQuery(id+"F5.opRevolve","SWEPT_FACE",FACE,{"disambiguationData":[OSD([sQuery(id+"F4.wireOp",EDGE,"E147.bottom")])]})]});
            var Q202;
            Q202=makeQuery(id+"F5.boolean.opBoolean","INTERSECT",EDGE,{"derivedFrom":[makeQuery(id+"F1.opExtrude","SWEPT_FACE",FACE,{"disambiguationData":[OSD([sQuery(id+"F0.wireOp",EDGE,"E68")])]}),makeQuery(id+"F5.opRevolve","SWEPT_FACE",FACE,{"disambiguationData":[OSD([sQuery(id+"F4.wireOp",EDGE,"E147.bottom")])]})]});
            var Q203;
            Q203=makeQuery(id+"F5.boolean.opBoolean","INTERSECT",EDGE,{"derivedFrom":[makeQuery(id+"F1.opExtrude","SWEPT_FACE",FACE,{"disambiguationData":[OSD([sQuery(id+"F0.wireOp",EDGE,"E68")])]}),makeQuery(id+"F5.opRevolve","SWEPT_FACE",FACE,{"disambiguationData":[OSD([sQuery(id+"F4.wireOp",EDGE,"E147.top")])]})]});
            var Q204;
            Q204=makeQuery(id+"F5.boolean.opBoolean","INTERSECT",EDGE,{"derivedFrom":[makeQuery(id+"F1.opExtrude","SWEPT_FACE",FACE,{"disambiguationData":[OSD([sQuery(id+"F0.wireOp",EDGE,"E60")])]}),makeQuery(id+"F5.opRevolve","SWEPT_FACE",FACE,{"disambiguationData":[OSD([sQuery(id+"F4.wireOp",EDGE,"E147.top")])]})]});
            var Q205;
            Q205=makeQuery(id+"F5.boolean.opBoolean","INTERSECT",EDGE,{"derivedFrom":[makeQuery(id+"F1.opExtrude","SWEPT_FACE",FACE,{"disambiguationData":[OSD([sQuery(id+"F0.wireOp",EDGE,"E60")])]}),makeQuery(id+"F5.opRevolve","SWEPT_FACE",FACE,{"disambiguationData":[OSD([sQuery(id+"F4.wireOp",EDGE,"E147.bottom")])]})]});
            var Q206;
            Q206=makeQuery(id+"F5.boolean.opBoolean","INTERSECT",EDGE,{"derivedFrom":[makeQuery(id+"F1.opExtrude","SWEPT_FACE",FACE,{"disambiguationData":[OSD([sQuery(id+"F0.wireOp",EDGE,"E52")])]}),makeQuery(id+"F5.opRevolve","SWEPT_FACE",FACE,{"disambiguationData":[OSD([sQuery(id+"F4.wireOp",EDGE,"E147.bottom")])]})]});
            var Q207;
            Q207=makeQuery(id+"F5.boolean.opBoolean","INTERSECT",EDGE,{"derivedFrom":[makeQuery(id+"F1.opExtrude","SWEPT_FACE",FACE,{"disambiguationData":[OSD([sQuery(id+"F0.wireOp",EDGE,"E52")])]}),makeQuery(id+"F5.opRevolve","SWEPT_FACE",FACE,{"disambiguationData":[OSD([sQuery(id+"F4.wireOp",EDGE,"E147.top")])]})]});
            var Q208;
            Q208=makeQuery(id+"F5.boolean.opBoolean","INTERSECT",EDGE,{"derivedFrom":[makeQuery(id+"F1.opExtrude","SWEPT_FACE",FACE,{"disambiguationData":[OSD([sQuery(id+"F0.wireOp",EDGE,"E44")])]}),makeQuery(id+"F5.opRevolve","SWEPT_FACE",FACE,{"disambiguationData":[OSD([sQuery(id+"F4.wireOp",EDGE,"E147.bottom")])]})]});
            var Q209;
            Q209=makeQuery(id+"F5.boolean.opBoolean","INTERSECT",EDGE,{"derivedFrom":[makeQuery(id+"F1.opExtrude","SWEPT_FACE",FACE,{"disambiguationData":[OSD([sQuery(id+"F0.wireOp",EDGE,"E44")])]}),makeQuery(id+"F5.opRevolve","SWEPT_FACE",FACE,{"disambiguationData":[OSD([sQuery(id+"F4.wireOp",EDGE,"E147.top")])]})]});
            var Q210;
            Q210=makeQuery(id+"F5.boolean.opBoolean","INTERSECT",EDGE,{"derivedFrom":[makeQuery(id+"F1.opExtrude","SWEPT_FACE",FACE,{"disambiguationData":[OSD([sQuery(id+"F0.wireOp",EDGE,"E36")])]}),makeQuery(id+"F5.opRevolve","SWEPT_FACE",FACE,{"disambiguationData":[OSD([sQuery(id+"F4.wireOp",EDGE,"E147.top")])]})]});
            var Q211;
            Q211=makeQuery(id+"F5.boolean.opBoolean","INTERSECT",EDGE,{"derivedFrom":[makeQuery(id+"F1.opExtrude","SWEPT_FACE",FACE,{"disambiguationData":[OSD([sQuery(id+"F0.wireOp",EDGE,"E36")])]}),makeQuery(id+"F5.opRevolve","SWEPT_FACE",FACE,{"disambiguationData":[OSD([sQuery(id+"F4.wireOp",EDGE,"E147.bottom")])]})]});
            var Q212;
            Q212=makeQuery(id+"F5.boolean.opBoolean","INTERSECT",EDGE,{"derivedFrom":[makeQuery(id+"F1.opExtrude","SWEPT_FACE",FACE,{"disambiguationData":[OSD([sQuery(id+"F0.wireOp",EDGE,"E28")])]}),makeQuery(id+"F5.opRevolve","SWEPT_FACE",FACE,{"disambiguationData":[OSD([sQuery(id+"F4.wireOp",EDGE,"E147.bottom")])]})]});
            var Q213;
            Q213=makeQuery(id+"F5.boolean.opBoolean","INTERSECT",EDGE,{"derivedFrom":[makeQuery(id+"F1.opExtrude","SWEPT_FACE",FACE,{"disambiguationData":[OSD([sQuery(id+"F0.wireOp",EDGE,"E28")])]}),makeQuery(id+"F5.opRevolve","SWEPT_FACE",FACE,{"disambiguationData":[OSD([sQuery(id+"F4.wireOp",EDGE,"E147.top")])]})]});
            var Q214;
            Q214=makeQuery(id+"F5.boolean.opBoolean","INTERSECT",EDGE,{"derivedFrom":[makeQuery(id+"F1.opExtrude","SWEPT_FACE",FACE,{"disambiguationData":[OSD([sQuery(id+"F0.wireOp",EDGE,"E30")])]}),makeQuery(id+"F5.opRevolve","SWEPT_FACE",FACE,{"disambiguationData":[OSD([sQuery(id+"F4.wireOp",EDGE,"E147.bottom")])]})]});
            var Q215;
            Q215=makeQuery(id+"F5.boolean.opBoolean","INTERSECT",EDGE,{"derivedFrom":[makeQuery(id+"F1.opExtrude","SWEPT_FACE",FACE,{"disambiguationData":[OSD([sQuery(id+"F0.wireOp",EDGE,"E30")])]}),makeQuery(id+"F5.opRevolve","SWEPT_FACE",FACE,{"disambiguationData":[OSD([sQuery(id+"F4.wireOp",EDGE,"E147.top")])]})]});
            var Q216;
            Q216=makeQuery(id+"F5.boolean.opBoolean","INTERSECT",EDGE,{"derivedFrom":[makeQuery(id+"F1.opExtrude","SWEPT_FACE",FACE,{"disambiguationData":[OSD([sQuery(id+"F0.wireOp",EDGE,"E20")])]}),makeQuery(id+"F5.opRevolve","SWEPT_FACE",FACE,{"disambiguationData":[OSD([sQuery(id+"F4.wireOp",EDGE,"E147.bottom")])]})]});
            var Q217;
            Q217=makeQuery(id+"F5.boolean.opBoolean","INTERSECT",EDGE,{"derivedFrom":[makeQuery(id+"F1.opExtrude","SWEPT_FACE",FACE,{"disambiguationData":[OSD([sQuery(id+"F0.wireOp",EDGE,"E20")])]}),makeQuery(id+"F5.opRevolve","SWEPT_FACE",FACE,{"disambiguationData":[OSD([sQuery(id+"F4.wireOp",EDGE,"E147.top")])]})]});
            chamfer(context, id + "F6", {"entities" : qUnion([Q0, Q1, Q2, Q3, Q4, Q5, Q6, Q7, Q8, Q9, Q10, Q11, Q12, Q13, Q14, Q15, Q16, Q17, Q18, Q19, Q20, Q21, Q22, Q23, Q24, Q25, Q26, Q27, Q28, Q29, Q30, Q31, Q32, Q33, Q34, Q35, Q36, Q37, Q38, Q39, Q40, Q41, Q42, Q43, Q44, Q45, Q46, Q47, Q48, Q49, Q50, Q51, Q52, Q53, Q54, Q55, Q56, Q57, Q58, Q59, Q60, Q61, Q62, Q63, Q64, Q65, Q66, Q67, Q68, Q69, Q70, Q71, Q72, Q73, Q74, Q75, Q76, Q77, Q78, Q79, Q80, Q81, Q82, Q83, Q84, Q85, Q86, Q87, Q88, Q89, Q90, Q91, Q92, Q93, Q94, Q95, Q96, Q97, Q98, Q99, Q100, Q101, Q102, Q103, Q104, Q105, Q106, Q107, Q108, Q109, Q110, Q111, Q112, Q113, Q114, Q115, Q116, Q117, Q118, Q119, Q120, Q121, Q122, Q123, Q124, Q125, Q126, Q127, Q128, Q129, Q130, Q131, Q132, Q133, Q134, Q135, Q136, Q137, Q138, Q139, Q140, Q141, Q142, Q143, Q144, Q145, Q146, Q147, Q148, Q149, Q150, Q151, Q152, Q153, Q154, Q155, Q156, Q157, Q158, Q159, Q160, Q161, Q162, Q163, Q164, Q165, Q166, Q167, Q168, Q169, Q170, Q171, Q172, Q173, Q174, Q175, Q176, Q177, Q178, Q179, Q180, Q181, Q182, Q183, Q184, Q185, Q186, Q187, Q188, Q189, Q190, Q191, Q192, Q193, Q194, Q195, Q196, Q197, Q198, Q199, Q200, Q201, Q202, Q203, Q204, Q205, Q206, Q207, Q208, Q209, Q210, Q211, Q212, Q213, Q214, Q215, Q216, Q217]), "width" : 1 * mm, "tangentPropagation" : true});
        }
    });
